# Revit family: Axis-FP
name_source: partatom
category: Оборудование
units: mm (PartAtom-declared; Revit-internal decimal feet)

## family parameters
Всегда вертикально = Да
Классификация = Нет
На основе рабочей плоскости = Нет
Общий = Нет
При загрузке вырезать с полостями = Нет
Размер круглого соединителя = Использовать диаметр
Тип детали = Нормальный
Точка принадлежности помещению = Нет

## types (239) — shared parameters
00_20_Manufacturer = BLAUBERG
00_20_Name = Axial smoke extraction fan
Casing Material = Metal, painted, grey, matt RAL 7040
Frequency = 50 Гц
Load Classification = HVAC
Maintenance zone material = <По категории>
Number of Fase = 3
Voltage = 400 В
Изготовитель = BLAUBERG
zero-valued in all types: Отметка по умолчанию

## per-type parameters (varying)
- Axis-FP-400-2D/0,55-6/25/AL: D1=450 мм; D2=490 мм; Diameter=400 мм; Dn=404 мм; Dv=390 мм; Dy=400 мм; Height=400 мм; L=400 мм; Ld=120 мм; Length=490 мм; Lv=105 мм; Maximum Air Flow=5004.0 м³/ч; Motor=Motor : 0.55 kW; N=6; P=240 мм; Power=550 Вт; W=525 мм; W1=475 мм; Weight=23.00 кг; Width=525 мм; d=8 мм; l=200 мм; l1=-200 мм; n=12; r1=225 мм
- Axis-FP-1250-4D/18,5-8/23/AL: D1=1320 мм; D2=1400 мм; Diameter=1250 мм; Dn=1254 мм; Dv=1240 мм; Dy=1250 мм; Height=750 мм; L=750 мм; Ld=225 мм; Length=1400 мм; Lv=210 мм; Maximum Air Flow=77040.0 м³/ч; Motor=Motor : 18.5 kW; N=8; P=665 мм; Power=18500 Вт; W=1450 мм; W1=1400 мм; Weight=335.00 кг; Width=1450 мм; d=15 мм; l=375 мм; l1=-375 мм; n=20; r1=660 мм
- Axis-FP-500-2D/1,1-6/25/AL: D1=560 мм; D2=600 мм; Diameter=500 мм; Dn=504 мм; Dv=490 мм; Dy=500 мм; Height=400 мм; L=400 мм; Ld=120 мм; Length=600 мм; Lv=105 мм; Maximum Air Flow=7920.0 м³/ч; Motor=Motor : 1.1 kW; N=6; P=290 мм; Power=1100 Вт; W=620 мм; W1=570 мм; Weight=32.00 кг; Width=620 мм; d=12 мм; l=200 мм; l1=-200 мм; n=12; r1=280 мм
- Axis-FP-560-2D/1,1-6/25/AL: D1=620 мм; D2=660 мм; Diameter=560 мм; Dn=564 мм; Dv=550 мм; Dy=560 мм; Height=400 мм; L=400 мм; Ld=120 мм; Length=660 мм; Lv=105 мм; Maximum Air Flow=9540.0 м³/ч; Motor=Motor : 1.1 kW; N=6; P=320 мм; Power=1100 Вт; W=680 мм; W1=630 мм; Weight=34.00 кг; Width=680 мм; d=12 мм; l=200 мм; l1=-200 мм; n=12; r1=310 мм
- Axis-FP-450-2D/0,75-6/25/AL: D1=500 мм; D2=540 мм; Diameter=450 мм; Dn=454 мм; Dv=440 мм; Dy=450 мм; Height=400 мм; L=400 мм; Ld=120 мм; Length=540 мм; Lv=105 мм; Maximum Air Flow=6480.0 м³/ч; Motor=Motor : 0.75 kW; N=6; P=265 мм; Power=750 Вт; W=580 мм; W1=530 мм; Weight=26.10 кг; Width=580 мм; d=8 мм; l=200 мм; l1=-200 мм; n=12; r1=250 мм
- Axis-FP-630-2D/2,2-6/25/AL: D1=690 мм; D2=730 мм; Diameter=630 мм; Dn=634 мм; Dv=620 мм; Dy=630 мм; Height=400 мм; L=400 мм; Ld=120 мм; Length=730 мм; Lv=105 мм; Maximum Air Flow=14040.0 м³/ч; Motor=Motor : 2.2kW; N=6; P=355 мм; Power=2200 Вт; W=750 мм; W1=700 мм; Weight=41.50 кг; Width=750 мм; d=12 мм; l=200 мм; l1=-200 мм; n=12; r1=345 мм
- Axis-FP-710-4D/0,75-6/20/AL: D1=770 мм; D2=810 мм; Diameter=710 мм; Dn=714 мм; Dv=700 мм; Dy=710 мм; Height=400 мм; L=400 мм; Ld=120 мм; Length=810 мм; Lv=105 мм; Maximum Air Flow=10440.0 м³/ч; Motor=Motor : 0.75 kW; N=6; P=395 мм; Power=750 Вт; W=845 мм; W1=795 мм; Weight=47.50 кг; Width=845 мм; d=12 мм; l=200 мм; l1=-200 мм; n=16; r1=385 мм
- Axis-FP-800-4D/1,1-6/20/AL: D1=860 мм; D2=900 мм; Diameter=800 мм; Dn=804 мм; Dv=790 мм; Dy=800 мм; Height=400 мм; L=400 мм; Ld=120 мм; Length=900 мм; Lv=105 мм; Maximum Air Flow=14040.0 м³/ч; Motor=Motor : 1.1 kW; N=6; P=440 мм; Power=1100 Вт; W=925 мм; W1=875 мм; Weight=59.50 кг; Width=925 мм; d=12 мм; l=200 мм; l1=-200 мм; n=16; r1=430 мм
- Axis-FP-900-4D/3-8/23,5/AL: D1=970 мм; D2=1015 мм; Diameter=900 мм; Dn=904 мм; Dv=890 мм; Dy=900 мм; Height=550 мм; L=550 мм; Ld=165 мм; Length=1015 мм; Lv=150 мм; Maximum Air Flow=23400.0 м³/ч; Motor=Motor : 3 kW; N=8; P=490 мм; Power=3000 Вт; W=1025 мм; W1=975 мм; Weight=92.00 кг; Width=1025 мм; d=15 мм; l=275 мм; l1=-275 мм; n=16; r1=485 мм
- Axis-FP-1000-4D/5,5-6/24/AL: D1=1070 мм; D2=1115 мм; Diameter=1000 мм; Dn=1004 мм; Dv=990 мм; Dy=1000 мм; Height=600 мм; L=600 мм; Ld=180 мм; Length=1115 мм; Lv=165 мм; Maximum Air Flow=36000.0 м³/ч; Motor=Motor : 5.5 kW; N=6; P=540 мм; Power=5500 Вт; W=1140 мм; W1=1090 мм; Weight=147.50 кг; Width=1140 мм; d=15 мм; l=300 мм; l1=-300 мм; n=16; r1=535 мм
- Axis-FP-1120-4D/7,5-6/23/AL: D1=1190 мм; D2=1270 мм; Diameter=1120 мм; Dn=1124 мм; Dv=1110 мм; Dy=1120 мм; Height=600 мм; L=600 мм; Ld=180 мм; Length=1270 мм; Lv=165 мм; Maximum Air Flow=46800.0 м³/ч; Motor=Motor : 7.5 kW; N=6; P=600 мм; Power=7500 Вт; W=1280 мм; W1=1230 мм; Weight=183.00 кг; Width=1280 мм; d=15 мм; l=300 мм; l1=-300 мм; n=20; r1=595 мм
- Axis-FP-400-2D/0,75-6/30/AL: D1=450 мм; D2=490 мм; Diameter=400 мм; Dn=404 мм; Dv=390 мм; Dy=400 мм; Height=400 мм; L=400 мм; Ld=120 мм; Length=490 мм; Lv=105 мм; Maximum Air Flow=5760.0 м³/ч; Motor=Motor : 0.75 kW; N=6; P=240 мм; Power=750 Вт; W=525 мм; W1=475 мм; Weight=24.60 кг; Width=525 мм; d=8 мм; l=200 мм; l1=-200 мм; n=12; r1=225 мм
- Axis-FP-400-2D/1,1-6/35/AL: D1=450 мм; D2=490 мм; Diameter=400 мм; Dn=404 мм; Dv=390 мм; Dy=400 мм; Height=400 мм; L=400 мм; Ld=120 мм; Length=490 мм; Lv=105 мм; Maximum Air Flow=6660.0 м³/ч; Motor=Motor : 1.1 kW; N=6; P=240 мм; Power=1100 Вт; W=525 мм; W1=475 мм; Weight=28.60 кг; Width=525 мм; d=8 мм; l=200 мм; l1=-200 мм; n=12; r1=225 мм
- Axis-FP-400-2D/1,5-6/40/AL: D1=450 мм; D2=490 мм; Diameter=400 мм; Dn=404 мм; Dv=390 мм; Dy=400 мм; Height=400 мм; L=400 мм; Ld=120 мм; Length=490 мм; Lv=105 мм; Maximum Air Flow=7200.0 м³/ч; Motor=Motor : 1.5kW; N=6; P=240 мм; Power=1500 Вт; W=525 мм; W1=475 мм; Weight=30.10 кг; Width=525 мм; d=8 мм; l=200 мм; l1=-200 мм; n=12; r1=225 мм
- Axis-FP-400-2D/1,5-6/45/AL: D1=450 мм; D2=490 мм; Diameter=400 мм; Dn=404 мм; Dv=390 мм; Dy=400 мм; Height=400 мм; L=400 мм; Ld=120 мм; Length=490 мм; Lv=105 мм; Maximum Air Flow=7920.0 м³/ч; Motor=Motor : 1.5kW; N=6; P=240 мм; Power=1500 Вт; W=525 мм; W1=475 мм; Weight=30.10 кг; Width=525 мм; d=8 мм; l=200 мм; l1=-200 мм; n=12; r1=225 мм
- Axis-FP-400-2D/2,2-8/45/AL: D1=450 мм; D2=490 мм; Diameter=400 мм; Dn=404 мм; Dv=390 мм; Dy=400 мм; Height=400 мм; L=400 мм; Ld=120 мм; Length=490 мм; Lv=105 мм; Maximum Air Flow=8280.0 м³/ч; Motor=Motor : 2.2kW; N=8; P=240 мм; Power=2200 Вт; W=525 мм; W1=475 мм; Weight=32.60 кг; Width=525 мм; d=8 мм; l=200 мм; l1=-200 мм; n=12; r1=225 мм
- Axis-FP-400-4D/0,55-6/30/AL: D1=450 мм; D2=490 мм; Diameter=400 мм; Dn=404 мм; Dv=390 мм; Dy=400 мм; Height=400 мм; L=400 мм; Ld=120 мм; Length=490 мм; Lv=105 мм; Maximum Air Flow=2880.0 м³/ч; Motor=Motor : 0.55 kW; N=6; P=240 мм; Power=550 Вт; W=525 мм; W1=475 мм; Weight=24.50 кг; Width=525 мм; d=8 мм; l=200 мм; l1=-200 мм; n=12; r1=225 мм
- Axis-FP-400-4D/0,55-6/35/AL: D1=450 мм; D2=490 мм; Diameter=400 мм; Dn=404 мм; Dv=390 мм; Dy=400 мм; Height=400 мм; L=400 мм; Ld=120 мм; Length=490 мм; Lv=105 мм; Maximum Air Flow=3420.0 м³/ч; Motor=Motor : 0.55 kW; N=6; P=240 мм; Power=550 Вт; W=525 мм; W1=475 мм; Weight=24.50 кг; Width=525 мм; d=8 мм; l=200 мм; l1=-200 мм; n=12; r1=225 мм
- Axis-FP-400-4D/0,55-6/40/AL: D1=450 мм; D2=490 мм; Diameter=400 мм; Dn=404 мм; Dv=390 мм; Dy=400 мм; Height=400 мм; L=400 мм; Ld=120 мм; Length=490 мм; Lv=105 мм; Maximum Air Flow=3600.0 м³/ч; Motor=Motor : 0.55 kW; N=6; P=240 мм; Power=550 Вт; W=525 мм; W1=475 мм; Weight=24.50 кг; Width=525 мм; d=8 мм; l=200 мм; l1=-200 мм; n=12; r1=225 мм
- Axis-FP-400-4D/0,55-6/45/AL: D1=450 мм; D2=490 мм; Diameter=400 мм; Dn=404 мм; Dv=390 мм; Dy=400 мм; Height=400 мм; L=400 мм; Ld=120 мм; Length=490 мм; Lv=105 мм; Maximum Air Flow=3780.0 м³/ч; Motor=Motor : 0.55 kW; N=6; P=240 мм; Power=550 Вт; W=525 мм; W1=475 мм; Weight=24.50 кг; Width=525 мм; d=8 мм; l=200 мм; l1=-200 мм; n=12; r1=225 мм
- Axis-FP-400-4D/0,55-8/45/AL: D1=450 мм; D2=490 мм; Diameter=400 мм; Dn=404 мм; Dv=390 мм; Dy=400 мм; Height=400 мм; L=400 мм; Ld=120 мм; Length=490 мм; Lv=105 мм; Maximum Air Flow=4140.0 м³/ч; Motor=Motor : 0.55 kW; N=8; P=240 мм; Power=550 Вт; W=525 мм; W1=475 мм; Weight=25.00 кг; Width=525 мм; d=8 мм; l=200 мм; l1=-200 мм; n=12; r1=225 мм
- Axis-FP-400-2/4D/0,8/0,2-6/30/AL: D1=450 мм; D2=490 мм; Diameter=400 мм; Dn=404 мм; Dv=390 мм; Dy=400 мм; Height=400 мм; L=400 мм; Ld=120 мм; Length=490 мм; Lv=105 мм; Maximum Air Flow=5760.0 м³/ч; Motor=Motor : 0.8 kW; N=6; P=240 мм; Power=800 Вт; W=525 мм; W1=475 мм; Weight=29.10 кг; Width=525 мм; d=8 мм; l=200 мм; l1=-200 мм; n=12; r1=225 мм
- Axis-FP-400-2/4D/1,1/0,25-6/35/AL: D1=450 мм; D2=490 мм; Diameter=400 мм; Dn=404 мм; Dv=390 мм; Dy=400 мм; Height=400 мм; L=400 мм; Ld=120 мм; Length=490 мм; Lv=105 мм; Maximum Air Flow=6660.0 м³/ч; Motor=Motor : 1.1 kW; N=6; P=240 мм; Power=1100 Вт; W=525 мм; W1=475 мм; Weight=30.10 кг; Width=525 мм; d=8 мм; l=200 мм; l1=-200 мм; n=12; r1=225 мм
- Axis-FP-400-2/4D/1,5/0,37-6/40/AL: D1=450 мм; D2=490 мм; Diameter=400 мм; Dn=404 мм; Dv=390 мм; Dy=400 мм; Height=400 мм; L=400 мм; Ld=120 мм; Length=490 мм; Lv=105 мм; Maximum Air Flow=7200.0 м³/ч; Motor=Motor : 1.5kW; N=6; P=240 мм; Power=1100 Вт; W=525 мм; W1=475 мм; Weight=35.80 кг; Width=525 мм; d=8 мм; l=200 мм; l1=-200 мм; n=12; r1=225 мм
- Axis-FP-400-2/4D/1,5/0,37-6/45/AL: D1=450 мм; D2=490 мм; Diameter=400 мм; Dn=404 мм; Dv=390 мм; Dy=400 мм; Height=400 мм; L=400 мм; Ld=120 мм; Length=490 мм; Lv=105 мм; Maximum Air Flow=7920.0 м³/ч; Motor=Motor : 1.5kW; N=6; P=240 мм; Power=1500 Вт; W=525 мм; W1=475 мм; Weight=35.80 кг; Width=525 мм; d=8 мм; l=200 мм; l1=-200 мм; n=12; r1=225 мм
- Axis-FP-400-2/4D/2,2/0,5-8/45/AL: D1=450 мм; D2=490 мм; Diameter=400 мм; Dn=404 мм; Dv=390 мм; Dy=400 мм; Height=400 мм; L=400 мм; Ld=120 мм; Length=490 мм; Lv=105 мм; Maximum Air Flow=8100.0 м³/ч; Motor=Motor : 2.2kW; N=8; P=240 мм; Power=2200 Вт; W=525 мм; W1=475 мм; Weight=38.00 кг; Width=525 мм; d=8 мм; l=200 мм; l1=-200 мм; n=12; r1=225 мм
- Axis-FP-450-2D/1,1-6/30/AL: D1=500 мм; D2=540 мм; Diameter=450 мм; Dn=454 мм; Dv=440 мм; Dy=450 мм; Height=400 мм; L=400 мм; Ld=120 мм; Length=540 мм; Lv=105 мм; Maximum Air Flow=7812.0 м³/ч; Motor=Motor : 1.1 kW; N=6; P=265 мм; Power=1100 Вт; W=580 мм; W1=530 мм; Weight=30.10 кг; Width=580 мм; d=8 мм; l=200 мм; l1=-200 мм; n=12; r1=250 мм
- Axis-FP-450-2D/1,5-6/35/AL: D1=500 мм; D2=540 мм; Diameter=450 мм; Dn=454 мм; Dv=440 мм; Dy=450 мм; Height=400 мм; L=400 мм; Ld=120 мм; Length=540 мм; Lv=105 мм; Maximum Air Flow=9360.0 м³/ч; Motor=Motor : 1.5kW; N=6; P=265 мм; Power=1500 Вт; W=580 мм; W1=530 мм; Weight=31.60 кг; Width=580 мм; d=8 мм; l=200 мм; l1=-200 мм; n=12; r1=250 мм
- Axis-FP-450-2D/2,2-6/40/AL: D1=500 мм; D2=540 мм; Diameter=450 мм; Dn=454 мм; Dv=440 мм; Dy=450 мм; Height=400 мм; L=400 мм; Ld=120 мм; Length=540 мм; Lv=105 мм; Maximum Air Flow=10080.0 м³/ч; Motor=Motor : 2.2kW; N=6; P=265 мм; Power=2200 Вт; W=580 мм; W1=530 мм; Weight=34.00 кг; Width=580 мм; d=8 мм; l=200 мм; l1=-200 мм; n=12; r1=250 мм
- Axis-FP-450-2D/3-8/40/AL: D1=500 мм; D2=540 мм; Diameter=450 мм; Dn=454 мм; Dv=440 мм; Dy=450 мм; Height=400 мм; L=400 мм; Ld=120 мм; Length=540 мм; Lv=105 мм; Maximum Air Flow=10440.0 м³/ч; Motor=Motor : 3 kW; N=6; P=265 мм; Power=3000 Вт; W=580 мм; W1=530 мм; Weight=34.00 кг; Width=580 мм; d=8 мм; l=200 мм; l1=-200 мм; n=12; r1=250 мм
- Axis-FP-450-2D/4-8/45/AL: D1=500 мм; D2=540 мм; Diameter=450 мм; Dn=454 мм; Dv=440 мм; Dy=450 мм; Height=400 мм; L=400 мм; Ld=120 мм; Length=540 мм; Lv=105 мм; Maximum Air Flow=11880.0 м³/ч; Motor=Motor : 3 kW; N=8; P=265 мм; Power=4000 Вт; W=580 мм; W1=530 мм; Weight=52.80 кг; Width=580 мм; d=8 мм; l=200 мм; l1=-200 мм; n=12; r1=250 мм
- Axis-FP-450-4D/0,55-6/25/AL: D1=500 мм; D2=540 мм; Diameter=450 мм; Dn=454 мм; Dv=440 мм; Dy=450 мм; Height=400 мм; L=400 мм; Ld=120 мм; Length=540 мм; Lv=105 мм; Maximum Air Flow=2304.0 м³/ч; Motor=Motor : 0.55 kW; N=6; P=265 мм; Power=550 Вт; W=580 мм; W1=530 мм; Weight=24.60 кг; Width=580 мм; d=8 мм; l=200 мм; l1=-200 мм; n=12; r1=250 мм
- Axis-FP-450-4D/0,55-6/30/AL: D1=500 мм; D2=540 мм; Diameter=450 мм; Dn=454 мм; Dv=440 мм; Dy=450 мм; Height=400 мм; L=400 мм; Ld=120 мм; Length=540 мм; Lv=105 мм; Maximum Air Flow=3780.0 м³/ч; Motor=Motor : 0.55 kW; N=6; P=265 мм; Power=550 Вт; W=580 мм; W1=530 мм; Weight=24.60 кг; Width=580 мм; d=8 мм; l=200 мм; l1=-200 мм; n=12; r1=250 мм
- Axis-FP-450-4D/0,55-6/35/AL: D1=500 мм; D2=540 мм; Diameter=450 мм; Dn=454 мм; Dv=440 мм; Dy=450 мм; Height=400 мм; L=400 мм; Ld=120 мм; Length=540 мм; Lv=105 мм; Maximum Air Flow=4500.0 м³/ч; Motor=Motor : 0.55 kW; N=6; P=265 мм; Power=550 Вт; W=580 мм; W1=530 мм; Weight=24.60 кг; Width=580 мм; d=8 мм; l=200 мм; l1=-200 мм; n=12; r1=250 мм
- Axis-FP-450-4D/0,55-6/40/AL: D1=500 мм; D2=540 мм; Diameter=450 мм; Dn=454 мм; Dv=440 мм; Dy=450 мм; Height=400 мм; L=400 мм; Ld=120 мм; Length=540 мм; Lv=105 мм; Maximum Air Flow=5040.0 м³/ч; Motor=Motor : 0.55 kW; N=6; P=265 мм; Power=550 Вт; W=580 мм; W1=530 мм; Weight=24.60 кг; Width=580 мм; d=8 мм; l=200 мм; l1=-200 мм; n=12; r1=250 мм
- Axis-FP-450-4D/0,55-8/40/AL: D1=500 мм; D2=540 мм; Diameter=450 мм; Dn=454 мм; Dv=440 мм; Dy=450 мм; Height=400 мм; L=400 мм; Ld=120 мм; Length=540 мм; Lv=105 мм; Maximum Air Flow=5220.0 м³/ч; Motor=Motor : 0.55 kW; N=8; P=265 мм; Power=550 Вт; W=580 мм; W1=530 мм; Weight=24.60 кг; Width=580 мм; d=8 мм; l=200 мм; l1=-200 мм; n=12; r1=250 мм
- Axis-FP-450-4D/0,55-8/45/AL: D1=500 мм; D2=540 мм; Diameter=450 мм; Dn=454 мм; Dv=440 мм; Dy=450 мм; Height=400 мм; L=400 мм; Ld=120 мм; Length=540 мм; Lv=105 мм; Maximum Air Flow=5940.0 м³/ч; Motor=Motor : 0.55 kW; N=8; P=265 мм; Power=550 Вт; W=580 мм; W1=530 мм; Weight=24.60 кг; Width=580 мм; d=8 мм; l=200 мм; l1=-200 мм; n=12; r1=250 мм
- Axis-FP-450-2/4D/4,4/1,1-8/45/AL: D1=500 мм; D2=540 мм; Diameter=450 мм; Dn=454 мм; Dv=440 мм; Dy=450 мм; Height=400 мм; L=400 мм; Ld=120 мм; Length=540 мм; Lv=105 мм; Maximum Air Flow=11880.0 м³/ч; Motor=Motor : 4.4 kW; N=8; P=265 мм; Power=4400 Вт; W=580 мм; W1=530 мм; Weight=63.80 кг; Width=580 мм; d=8 мм; l=200 мм; l1=-200 мм; n=12; r1=250 мм
- Axis-FP-450-2/4D/3,1/0,8-8/40/AL: D1=500 мм; D2=540 мм; Diameter=450 мм; Dn=454 мм; Dv=440 мм; Dy=450 мм; Height=400 мм; L=400 мм; Ld=120 мм; Length=540 мм; Lv=105 мм; Maximum Air Flow=10440.0 м³/ч; Motor=Motor : 3.1 kW; N=8; P=265 мм; Power=3100 Вт; W=580 мм; W1=530 мм; Weight=51.90 кг; Width=580 мм; d=8 мм; l=200 мм; l1=-200 мм; n=12; r1=250 мм
- Axis-FP-450-2/4D/2,2/0,5-6/40/AL: D1=500 мм; D2=540 мм; Diameter=450 мм; Dn=454 мм; Dv=440 мм; Dy=450 мм; Height=400 мм; L=400 мм; Ld=120 мм; Length=540 мм; Lv=105 мм; Maximum Air Flow=10080.0 м³/ч; Motor=Motor : 2.2kW; N=6; P=265 мм; Power=2200 Вт; W=580 мм; W1=530 мм; Weight=39.30 кг; Width=580 мм; d=8 мм; l=200 мм; l1=-200 мм; n=12; r1=250 мм
- Axis-FP-450-2/4D/1,5/0,37-6/35/AL: D1=500 мм; D2=540 мм; Diameter=450 мм; Dn=454 мм; Dv=440 мм; Dy=450 мм; Height=400 мм; L=400 мм; Ld=120 мм; Length=540 мм; Lv=105 мм; Maximum Air Flow=9000.0 м³/ч; Motor=Motor : 1.5kW; N=6; P=265 мм; Power=1500 Вт; W=580 мм; W1=530 мм; Weight=37.30 кг; Width=580 мм; d=8 мм; l=200 мм; l1=-200 мм; n=12; r1=250 мм
- Axis-FP-450-2/4D/1,1/0,25-6/30/AL: D1=500 мм; D2=540 мм; Diameter=450 мм; Dn=454 мм; Dv=440 мм; Dy=450 мм; Height=400 мм; L=400 мм; Ld=120 мм; Length=540 мм; Lv=105 мм; Maximum Air Flow=7740.0 м³/ч; Motor=Motor : 1.1 kW; N=6; P=265 мм; Power=1100 Вт; W=580 мм; W1=530 мм; Weight=31.60 кг; Width=580 мм; d=8 мм; l=200 мм; l1=-200 мм; n=12; r1=250 мм
- Axis-FP-450-2/4D/0,8/0,2-6/25/AL: D1=500 мм; D2=540 мм; Diameter=450 мм; Dn=454 мм; Dv=440 мм; Dy=450 мм; Height=400 мм; L=400 мм; Ld=120 мм; Length=540 мм; Lv=105 мм; Maximum Air Flow=6480.0 м³/ч; Motor=Motor : 0.8 kW; N=6; P=265 мм; Power=800 Вт; W=580 мм; W1=530 мм; Weight=30.60 кг; Width=580 мм; d=8 мм; l=200 мм; l1=-200 мм; n=12; r1=250 мм
- Axis-FP-500-2D/1,5-6/30/AL: D1=560 мм; D2=600 мм; Diameter=500 мм; Dn=504 мм; Dv=490 мм; Dy=500 мм; Height=400 мм; L=400 мм; Ld=120 мм; Length=600 мм; Lv=105 мм; Maximum Air Flow=9540.0 м³/ч; Motor=Motor : 1.5kW; N=6; P=290 мм; Power=1500 Вт; W=620 мм; W1=570 мм; Weight=33.50 кг; Width=620 мм; d=12 мм; l=200 мм; l1=-200 мм; n=12; r1=280 мм
- Axis-FP-500-2D/2,2-6/35/AL: D1=560 мм; D2=600 мм; Diameter=500 мм; Dn=504 мм; Dv=490 мм; Dy=500 мм; Height=400 мм; L=400 мм; Ld=120 мм; Length=600 мм; Lv=105 мм; Maximum Air Flow=11520.0 м³/ч; Motor=Motor : 2.2kW; N=6; P=290 мм; Power=2200 Вт; W=620 мм; W1=570 мм; Weight=36.00 кг; Width=620 мм; d=12 мм; l=200 мм; l1=-200 мм; n=12; r1=280 мм
- Axis-FP-500-2D/3-8/35/AL: D1=560 мм; D2=600 мм; Diameter=500 мм; Dn=504 мм; Dv=490 мм; Dy=500 мм; Height=400 мм; L=400 мм; Ld=120 мм; Length=600 мм; Lv=105 мм; Maximum Air Flow=12600.0 м³/ч; Motor=Motor : 3 kW; N=8; P=290 мм; Power=3000 Вт; W=620 мм; W1=570 мм; Weight=43.00 кг; Width=620 мм; d=12 мм; l=200 мм; l1=-200 мм; n=12; r1=280 мм
- Axis-FP-500-2D/4-8/40/AL: D1=560 мм; D2=600 мм; Diameter=500 мм; Dn=504 мм; Dv=490 мм; Dy=500 мм; Height=500 мм; L=500 мм; Ld=150 мм; Length=600 мм; Lv=135 мм; Maximum Air Flow=14040.0 м³/ч; Motor=Motor : 4 kW; N=8; P=290 мм; Power=4000 Вт; W=620 мм; W1=570 мм; Weight=55.00 кг; Width=620 мм; d=12 мм; l=250 мм; l1=-250 мм; n=12; r1=280 мм
- Axis-FP-500-2D/5,5-8/45/AL: D1=560 мм; D2=600 мм; Diameter=500 мм; Dn=504 мм; Dv=490 мм; Dy=500 мм; Height=500 мм; L=500 мм; Ld=150 мм; Length=600 мм; Lv=135 мм; Maximum Air Flow=15480.0 м³/ч; Motor=Motor : 5.5 kW; N=8; P=290 мм; Power=5500 Вт; W=620 мм; W1=570 мм; Weight=63.00 кг; Width=620 мм; d=12 мм; l=250 мм; l1=-250 мм; n=12; r1=280 мм
- Axis-FP-500-4D/0,55-6/25/AL: D1=560 мм; D2=600 мм; Diameter=500 мм; Dn=504 мм; Dv=490 мм; Dy=500 мм; Height=400 мм; L=400 мм; Ld=120 мм; Length=600 мм; Lv=105 мм; Maximum Air Flow=3960.0 м³/ч; Motor=Motor : 0.55 kW; N=6; P=290 мм; Power=550 Вт; W=620 мм; W1=570 мм; Weight=28.00 кг; Width=620 мм; d=12 мм; l=200 мм; l1=-200 мм; n=12; r1=280 мм
- Axis-FP-500-4D/0,55-6/30/AL: D1=560 мм; D2=600 мм; Diameter=500 мм; Dn=504 мм; Dv=490 мм; Dy=500 мм; Height=400 мм; L=400 мм; Ld=120 мм; Length=600 мм; Lv=105 мм; Maximum Air Flow=4860.0 м³/ч; Motor=Motor : 0.55 kW; N=6; P=290 мм; Power=550 Вт; W=620 мм; W1=570 мм; Weight=28.00 кг; Width=620 мм; d=12 мм; l=200 мм; l1=-200 мм; n=12; r1=280 мм
- Axis-FP-500-4D/0,55-6/35/AL: D1=560 мм; D2=600 мм; Diameter=500 мм; Dn=504 мм; Dv=490 мм; Dy=500 мм; Height=400 мм; L=400 мм; Ld=120 мм; Length=600 мм; Lv=105 мм; Maximum Air Flow=5940.0 м³/ч; Motor=Motor : 0.55 kW; N=6; P=290 мм; Power=550 Вт; W=620 мм; W1=570 мм; Weight=28.00 кг; Width=620 мм; d=12 мм; l=200 мм; l1=-200 мм; n=12; r1=280 мм
- Axis-FP-500-4D/0,55-6/40/AL: D1=560 мм; D2=600 мм; Diameter=500 мм; Dn=504 мм; Dv=490 мм; Dy=500 мм; Height=400 мм; L=400 мм; Ld=120 мм; Length=600 мм; Lv=105 мм; Maximum Air Flow=6408.0 м³/ч; Motor=Motor : 0.55 kW; N=6; P=290 мм; Power=550 Вт; W=620 мм; W1=570 мм; Weight=28.00 кг; Width=620 мм; d=12 мм; l=200 мм; l1=-200 мм; n=12; r1=280 мм
- Axis-FP-500-4D/0,55-6/45/AL: D1=560 мм; D2=600 мм; Diameter=500 мм; Dn=504 мм; Dv=490 мм; Dy=500 мм; Height=400 мм; L=400 мм; Ld=120 мм; Length=600 мм; Lv=105 мм; Maximum Air Flow=7020.0 м³/ч; Motor=Motor : 0.55 kW; N=6; P=290 мм; Power=550 Вт; W=620 мм; W1=570 мм; Weight=28.00 кг; Width=620 мм; d=12 мм; l=200 мм; l1=-200 мм; n=12; r1=280 мм
- Axis-FP-500-4D/0,75-8/45/AL: D1=560 мм; D2=600 мм; Diameter=500 мм; Dn=504 мм; Dv=490 мм; Dy=500 мм; Height=400 мм; L=400 мм; Ld=120 мм; Length=600 мм; Lv=105 мм; Maximum Air Flow=7560.0 м³/ч; Motor=Motor : 0.75 kW; N=8; P=290 мм; Power=750 Вт; W=620 мм; W1=570 мм; Weight=29.50 кг; Width=620 мм; d=12 мм; l=200 мм; l1=-200 мм; n=12; r1=280 мм
- Axis-FP-500-2/4D/1,1/0,25-6/25/AL: D1=560 мм; D2=600 мм; Diameter=500 мм; Dn=504 мм; Dv=490 мм; Dy=500 мм; Height=400 мм; L=400 мм; Ld=120 мм; Length=600 мм; Lv=105 мм; Maximum Air Flow=7920.0 м³/ч; Motor=Motor : 1.1 kW; N=6; P=290 мм; Power=1100 Вт; W=620 мм; W1=570 мм; Weight=29.50 кг; Width=620 мм; d=12 мм; l=200 мм; l1=-200 мм; n=12; r1=280 мм
- Axis-FP-500-2/4D/1,5/0,37-6/30/AL: D1=560 мм; D2=600 мм; Diameter=500 мм; Dn=504 мм; Dv=490 мм; Dy=500 мм; Height=400 мм; L=400 мм; Ld=120 мм; Length=600 мм; Lv=105 мм; Maximum Air Flow=9540.0 м³/ч; Motor=Motor : 1.5kW; N=6; P=290 мм; Power=1500 Вт; W=620 мм; W1=570 мм; Weight=39.00 кг; Width=620 мм; d=12 мм; l=200 мм; l1=-200 мм; n=12; r1=280 мм
- Axis-FP-500-2/4D/2,2/0,5-6/35/AL: D1=560 мм; D2=600 мм; Diameter=500 мм; Dn=504 мм; Dv=490 мм; Dy=500 мм; Height=400 мм; L=400 мм; Ld=120 мм; Length=600 мм; Lv=105 мм; Maximum Air Flow=11520.0 м³/ч; Motor=Motor : 2.2kW; N=6; P=290 мм; Power=2200 Вт; W=620 мм; W1=570 мм; Weight=41.00 кг; Width=620 мм; d=12 мм; l=200 мм; l1=-200 мм; n=12; r1=280 мм
- Axis-FP-500-2/4D/3,1/0,8-8/35/AL: D1=560 мм; D2=600 мм; Diameter=500 мм; Dn=504 мм; Dv=490 мм; Dy=500 мм; Height=500 мм; L=500 мм; Ld=150 мм; Length=600 мм; Lv=135 мм; Maximum Air Flow=12960.0 м³/ч; Motor=Motor : 3.1 kW; N=8; P=290 мм; Power=3100 Вт; W=620 мм; W1=570 мм; Weight=54.00 кг; Width=620 мм; d=12 мм; l=250 мм; l1=-250 мм; n=12; r1=280 мм
- Axis-FP-500-2/4D/4,4/1,1-8/40/AL: D1=560 мм; D2=600 мм; Diameter=500 мм; Dn=504 мм; Dv=490 мм; Dy=500 мм; Height=500 мм; L=500 мм; Ld=150 мм; Length=600 мм; Lv=135 мм; Maximum Air Flow=14040.0 м³/ч; Motor=Motor : 4.4 kW; N=8; P=290 мм; Power=4400 Вт; W=620 мм; W1=570 мм; Weight=66.00 кг; Width=620 мм; d=12 мм; l=250 мм; l1=-250 мм; n=12; r1=280 мм
- Axis-FP-500-2/4D/6/1,5-8/45/AL: D1=560 мм; D2=600 мм; Diameter=500 мм; Dn=504 мм; Dv=490 мм; Dy=500 мм; Height=550 мм; L=550 мм; Ld=165 мм; Length=600 мм; Lv=150 мм; Maximum Air Flow=15480.0 м³/ч; Motor=Motor : 6 kW; N=8; P=290 мм; Power=6000 Вт; W=620 мм; W1=570 мм; Weight=85.00 кг; Width=620 мм; d=12 мм; l=275 мм; l1=-275 мм; n=12; r1=280 мм
- Axis-FP-560-2D/1,5-6/30/AL: D1=620 мм; D2=660 мм; Diameter=560 мм; Dn=564 мм; Dv=550 мм; Dy=560 мм; Height=400 мм; L=400 мм; Ld=120 мм; Length=660 мм; Lv=105 мм; Maximum Air Flow=11880.0 м³/ч; Motor=Motor : 1.5kW; N=6; P=320 мм; Power=1500 Вт; W=680 мм; W1=630 мм; Weight=35.50 кг; Width=680 мм; d=12 мм; l=200 мм; l1=-200 мм; n=12; r1=310 мм
- Axis-FP-560-2D/2,2-8/30/AL: D1=620 мм; D2=660 мм; Diameter=560 мм; Dn=564 мм; Dv=550 мм; Dy=560 мм; Height=400 мм; L=400 мм; Ld=120 мм; Length=660 мм; Lv=105 мм; Maximum Air Flow=13500.0 м³/ч; Motor=Motor : 2.2kW; N=8; P=320 мм; Power=2200 Вт; W=680 мм; W1=630 мм; Weight=38.00 кг; Width=680 мм; d=12 мм; l=200 мм; l1=-200 мм; n=12; r1=310 мм
- Axis-FP-560-2D/4-8/35/AL: D1=620 мм; D2=660 мм; Diameter=560 мм; Dn=564 мм; Dv=550 мм; Dy=560 мм; Height=500 мм; L=500 мм; Ld=150 мм; Length=660 мм; Lv=135 мм; Maximum Air Flow=16488.0 м³/ч; Motor=Motor : 4 kW; N=8; P=320 мм; Power=4000 Вт; W=680 мм; W1=630 мм; Weight=57.50 кг; Width=680 мм; d=12 мм; l=250 мм; l1=-250 мм; n=12; r1=310 мм
- Axis-FP-560-2D/5,5-8/40/AL: D1=620 мм; D2=660 мм; Diameter=560 мм; Dn=564 мм; Dv=550 мм; Dy=560 мм; Height=500 мм; L=500 мм; Ld=150 мм; Length=660 мм; Lv=135 мм; Maximum Air Flow=18000.0 м³/ч; Motor=Motor : 5.5 kW; N=8; P=320 мм; Power=5500 Вт; W=680 мм; W1=630 мм; Weight=65.50 кг; Width=680 мм; d=12 мм; l=250 мм; l1=-250 мм; n=12; r1=310 мм
- Axis-FP-560-2D/7,5-8/45/AL: D1=620 мм; D2=660 мм; Diameter=560 мм; Dn=564 мм; Dv=550 мм; Dy=560 мм; Height=500 мм; L=500 мм; Ld=150 мм; Length=660 мм; Lv=135 мм; Maximum Air Flow=20520.0 м³/ч; Motor=Motor : 7.5 kW; N=8; P=320 мм; Power=7500 Вт; W=680 мм; W1=630 мм; Weight=67.50 кг; Width=680 мм; d=12 мм; l=250 мм; l1=-250 мм; n=12; r1=310 мм
- Axis-FP-560-4D/0,55-6/25/AL: D1=620 мм; D2=660 мм; Diameter=560 мм; Dn=564 мм; Dv=550 мм; Dy=560 мм; Height=400 мм; L=400 мм; Ld=120 мм; Length=660 мм; Lv=105 мм; Maximum Air Flow=4860.0 м³/ч; Motor=Motor : 0.55 kW; N=6; P=320 мм; Power=550 Вт; W=680 мм; W1=630 мм; Weight=30.00 кг; Width=680 мм; d=12 мм; l=200 мм; l1=-200 мм; n=12; r1=310 мм
- Axis-FP-560-4D/0,55-6/30/AL: D1=620 мм; D2=660 мм; Diameter=560 мм; Dn=564 мм; Dv=550 мм; Dy=560 мм; Height=400 мм; L=400 мм; Ld=120 мм; Length=660 мм; Lv=105 мм; Maximum Air Flow=5940.0 м³/ч; Motor=Motor : 0.55 kW; N=6; P=320 мм; Power=550 Вт; W=680 мм; W1=630 мм; Weight=30.00 кг; Width=680 мм; d=12 мм; l=200 мм; l1=-200 мм; n=12; r1=310 мм
- Axis-FP-560-4D/0,55-6/35/AL: D1=620 мм; D2=660 мм; Diameter=560 мм; Dn=564 мм; Dv=550 мм; Dy=560 мм; Height=400 мм; L=400 мм; Ld=120 мм; Length=660 мм; Lv=105 мм; Maximum Air Flow=7380.0 м³/ч; Motor=Motor : 0.55 kW; N=6; P=320 мм; Power=550 Вт; W=680 мм; W1=630 мм; Weight=30.00 кг; Width=680 мм; d=12 мм; l=200 мм; l1=-200 мм; n=12; r1=310 мм
- Axis-FP-560-4D/0,55-6/40/AL: D1=620 мм; D2=660 мм; Diameter=560 мм; Dn=564 мм; Dv=550 мм; Dy=560 мм; Height=400 мм; L=400 мм; Ld=120 мм; Length=660 мм; Lv=105 мм; Maximum Air Flow=8280.0 м³/ч; Motor=Motor : 0.55 kW; N=6; P=320 мм; Power=550 Вт; W=680 мм; W1=630 мм; Weight=30.00 кг; Width=680 мм; d=12 мм; l=200 мм; l1=-200 мм; n=12; r1=310 мм
- Axis-FP-560-4D/0,55-6/45/AL: D1=620 мм; D2=660 мм; Diameter=560 мм; Dn=564 мм; Dv=550 мм; Dy=560 мм; Height=400 мм; L=400 мм; Ld=120 мм; Length=660 мм; Lv=105 мм; Maximum Air Flow=9000.0 м³/ч; Motor=Motor : 0.55 kW; N=6; P=320 мм; Power=550 Вт; W=680 мм; W1=630 мм; Weight=30.00 кг; Width=680 мм; d=12 мм; l=200 мм; l1=-200 мм; n=12; r1=310 мм
- Axis-FP-560-4D/0,75-8/45/AL: D1=620 мм; D2=660 мм; Diameter=560 мм; Dn=564 мм; Dv=550 мм; Dy=560 мм; Height=400 мм; L=400 мм; Ld=120 мм; Length=660 мм; Lv=105 мм; Maximum Air Flow=10260.0 м³/ч; Motor=Motor : 0.75 kW; N=8; P=320 мм; Power=750 Вт; W=680 мм; W1=630 мм; Weight=31.50 кг; Width=680 мм; d=12 мм; l=200 мм; l1=-200 мм; n=12; r1=310 мм
- Axis-FP-560-2/4D/1,1/0,25-6/25/AL: D1=620 мм; D2=660 мм; Diameter=560 мм; Dn=564 мм; Dv=550 мм; Dy=560 мм; Height=400 мм; L=400 мм; Ld=120 мм; Length=660 мм; Lv=105 мм; Maximum Air Flow=9720.0 м³/ч; Motor=Motor : 1.1 kW; N=6; P=320 мм; Power=1100 Вт; W=680 мм; W1=630 мм; Weight=35.50 кг; Width=680 мм; d=12 мм; l=200 мм; l1=-200 мм; n=12; r1=310 мм
- Axis-FP-560-2/4D/1,5/0,37-6/30/AL: D1=620 мм; D2=660 мм; Diameter=560 мм; Dn=564 мм; Dv=550 мм; Dy=560 мм; Height=400 мм; L=400 мм; Ld=120 мм; Length=660 мм; Lv=105 мм; Maximum Air Flow=11880.0 м³/ч; Motor=Motor : 1.5kW; N=6; P=320 мм; Power=1500 Вт; W=680 мм; W1=630 мм; Weight=41.00 кг; Width=680 мм; d=12 мм; l=200 мм; l1=-200 мм; n=12; r1=310 мм
- Axis-FP-560-2/4D/2,2/0,5-8/30/AL: D1=620 мм; D2=660 мм; Diameter=560 мм; Dn=564 мм; Dv=550 мм; Dy=560 мм; Height=400 мм; L=400 мм; Ld=120 мм; Length=660 мм; Lv=105 мм; Maximum Air Flow=13500.0 м³/ч; Motor=Motor : 2.2kW; N=8; P=320 мм; Power=2200 Вт; W=680 мм; W1=630 мм; Weight=43.50 кг; Width=680 мм; d=12 мм; l=200 мм; l1=-200 мм; n=12; r1=310 мм
- Axis-FP-560-2/4D/4,4/1,1-8/35/AL: D1=620 мм; D2=660 мм; Diameter=560 мм; Dn=564 мм; Dv=550 мм; Dy=560 мм; Height=500 мм; L=500 мм; Ld=150 мм; Length=660 мм; Lv=135 мм; Maximum Air Flow=16560.0 м³/ч; Motor=Motor : 4.4 kW; N=8; P=320 мм; Power=4400 Вт; W=680 мм; W1=630 мм; Weight=68.50 кг; Width=680 мм; d=12 мм; l=250 мм; l1=-250 мм; n=12; r1=310 мм
- Axis-FP-560-2/4D/6/1,5-8/40/AL: D1=620 мм; D2=660 мм; Diameter=560 мм; Dn=564 мм; Dv=550 мм; Dy=560 мм; Height=550 мм; L=550 мм; Ld=165 мм; Length=660 мм; Lv=150 мм; Maximum Air Flow=18000.0 м³/ч; Motor=Motor : 6 kW; N=8; P=320 мм; Power=6000 Вт; W=680 мм; W1=630 мм; Weight=96.50 кг; Width=680 мм; d=12 мм; l=275 мм; l1=-275 мм; n=12; r1=310 мм
- Axis-FP-560-2/4D/8/2-8/45/AL: D1=620 мм; D2=660 мм; Diameter=560 мм; Dn=564 мм; Dv=550 мм; Dy=560 мм; Height=550 мм; L=550 мм; Ld=165 мм; Length=660 мм; Lv=150 мм; Maximum Air Flow=20520.0 м³/ч; Motor=Motor : 8 кВт; N=8; P=320 мм; Power=8000 Вт; W=680 мм; W1=630 мм; Weight=105.50 кг; Width=680 мм; d=12 мм; l=275 мм; l1=-275 мм; n=12; r1=310 мм
- Axis-FP-630-2D/3-6/30/AL: D1=690 мм; D2=730 мм; Diameter=630 мм; Dn=634 мм; Dv=620 мм; Dy=630 мм; Height=400 мм; L=400 мм; Ld=120 мм; Length=730 мм; Lv=105 мм; Maximum Air Flow=16920.0 м³/ч; Motor=Motor : 3 kW; N=6; P=355 мм; Power=3000 Вт; W=750 мм; W1=700 мм; Weight=48.00 кг; Width=750 мм; d=12 мм; l=200 мм; l1=-200 мм; n=12; r1=345 мм
- Axis-FP-630-2D/4-7/32,5/AL: D1=690 мм; D2=730 мм; Diameter=630 мм; Dn=634 мм; Dv=620 мм; Dy=630 мм; Height=500 мм; L=500 мм; Ld=150 мм; Length=730 мм; Lv=135 мм; Maximum Air Flow=18900.0 м³/ч; Motor=Motor : 4 kW; N=7; P=355 мм; Power=4000 Вт; W=750 мм; W1=700 мм; Weight=61.50 кг; Width=750 мм; d=12 мм; l=250 мм; l1=-250 мм; n=12; r1=345 мм
- Axis-FP-630-2D/5,5-7/35/AL: D1=690 мм; D2=730 мм; Diameter=630 мм; Dn=634 мм; Dv=620 мм; Dy=630 мм; Height=500 мм; L=500 мм; Ld=150 мм; Length=730 мм; Lv=135 мм; Maximum Air Flow=21060.0 м³/ч; Motor=Motor : 5.5 kW; N=7; P=355 мм; Power=5500 Вт; W=750 мм; W1=700 мм; Weight=70.00 кг; Width=750 мм; d=12 мм; l=250 мм; l1=-250 мм; n=12; r1=345 мм
- Axis-FP-630-2D/5,5-7/37,5/AL: D1=690 мм; D2=730 мм; Diameter=630 мм; Dn=634 мм; Dv=620 мм; Dy=630 мм; Height=500 мм; L=500 мм; Ld=150 мм; Length=730 мм; Lv=135 мм; Maximum Air Flow=21960.0 м³/ч; Motor=Motor : 5.5 kW; N=7; P=355 мм; Power=5500 Вт; W=750 мм; W1=700 мм; Weight=70.00 кг; Width=750 мм; d=12 мм; l=250 мм; l1=-250 мм; n=12; r1=345 мм
- Axis-FP-630-2D/7,5-7/41,5/AL: D1=690 мм; D2=730 мм; Diameter=630 мм; Dn=634 мм; Dv=620 мм; Dy=630 мм; Height=500 мм; L=500 мм; Ld=150 мм; Length=730 мм; Lv=135 мм; Maximum Air Flow=21960.0 м³/ч; Motor=Motor : 7.5 kW; N=7; P=355 мм; Power=7500 Вт; W=750 мм; W1=700 мм; Weight=71.50 кг; Width=750 мм; d=12 мм; l=250 мм; l1=-250 мм; n=12; r1=345 мм
- Axis-FP-630-2D/11-8/41,5/AL: D1=690 мм; D2=730 мм; Diameter=630 мм; Dn=634 мм; Dv=620 мм; Dy=630 мм; Height=550 мм; L=550 мм; Ld=165 мм; Length=730 мм; Lv=150 мм; Maximum Air Flow=26100.0 м³/ч; Motor=Motor : 11 kW; N=8; P=355 мм; Power=11000 Вт; W=750 мм; W1=700 мм; Weight=119.50 кг; Width=750 мм; d=12 мм; l=275 мм; l1=-275 мм; n=12; r1=345 мм
- Axis-FP-630-2D/15-8/46,5/AL: D1=690 мм; D2=730 мм; Diameter=630 мм; Dn=634 мм; Dv=620 мм; Dy=630 мм; Height=700 мм; L=700 мм; Ld=210 мм; Length=730 мм; Lv=195 мм; Maximum Air Flow=28800.0 м³/ч; Motor=Motor : 15 kW; N=8; P=355 мм; Power=15000 Вт; W=750 мм; W1=700 мм; Weight=167.00 кг; Width=750 мм; d=12 мм; l=350 мм; l1=-350 мм; n=12; r1=345 мм
- Axis-FP-630-2D/15-9/48,5/AL: D1=690 мм; D2=730 мм; Diameter=630 мм; Dn=634 мм; Dv=620 мм; Dy=630 мм; Height=700 мм; L=700 мм; Ld=210 мм; Length=730 мм; Lv=195 мм; Maximum Air Flow=30060.0 м³/ч; Motor=Motor : 15 kW; N=9; P=355 мм; Power=15000 Вт; W=750 мм; W1=700 мм; Weight=166.00 кг; Width=750 мм; d=12 мм; l=350 мм; l1=-350 мм; n=12; r1=345 мм
- Axis-FP-630-4D/0,55-8/25/AL: D1=690 мм; D2=730 мм; Diameter=630 мм; Dn=634 мм; Dv=620 мм; Dy=630 мм; Height=400 мм; L=400 мм; Ld=120 мм; Length=730 мм; Lv=105 мм; Maximum Air Flow=6480.0 м³/ч; Motor=Motor : 0.55 kW; N=8; P=355 мм; Power=550 Вт; W=750 мм; W1=700 мм; Weight=31.50 кг; Width=750 мм; d=12 мм; l=200 мм; l1=-200 мм; n=12; r1=345 мм
- Axis-FP-630-4D/0,55-8/30/AL: D1=690 мм; D2=730 мм; Diameter=630 мм; Dn=634 мм; Dv=620 мм; Dy=630 мм; Height=400 мм; L=400 мм; Ld=120 мм; Length=730 мм; Lv=105 мм; Maximum Air Flow=8280.0 м³/ч; Motor=Motor : 0.55 kW; N=8; P=355 мм; Power=550 Вт; W=750 мм; W1=700 мм; Weight=31.50 кг; Width=750 мм; d=12 мм; l=200 мм; l1=-200 мм; n=12; r1=345 мм
- Axis-FP-630-4D/0,75-8/35/AL: D1=690 мм; D2=730 мм; Diameter=630 мм; Dn=634 мм; Dv=620 мм; Dy=630 мм; Height=400 мм; L=400 мм; Ld=120 мм; Length=730 мм; Lv=105 мм; Maximum Air Flow=10260.0 м³/ч; Motor=Motor : 0.75 kW; N=8; P=355 мм; Power=750 Вт; W=750 мм; W1=700 мм; Weight=32.50 кг; Width=750 мм; d=12 мм; l=200 мм; l1=-200 мм; n=12; r1=345 мм
- Axis-FP-630-4D/1,1-8/40/AL: D1=690 мм; D2=730 мм; Diameter=630 мм; Dn=634 мм; Dv=620 мм; Dy=630 мм; Height=400 мм; L=400 мм; Ld=120 мм; Length=730 мм; Lv=105 мм; Maximum Air Flow=11520.0 м³/ч; Motor=Motor : 1.1 kW; N=8; P=355 мм; Power=1100 Вт; W=750 мм; W1=700 мм; Weight=36.50 кг; Width=750 мм; d=12 мм; l=200 мм; l1=-200 мм; n=12; r1=345 мм
- Axis-FP-630-4D/1,1-6/32,5/AL: D1=690 мм; D2=730 мм; Diameter=630 мм; Dn=634 мм; Dv=620 мм; Dy=630 мм; Height=400 мм; L=400 мм; Ld=120 мм; Length=730 мм; Lv=105 мм; Maximum Air Flow=12780.0 м³/ч; Motor=Motor : 1.1 kW; N=6; P=355 мм; Power=1100 Вт; W=750 мм; W1=700 мм; Weight=38.50 кг; Width=750 мм; d=12 мм; l=200 мм; l1=-200 мм; n=12; r1=345 мм
- Axis-FP-630-4D/1,5-6/37,5/AL: D1=690 мм; D2=730 мм; Diameter=630 мм; Dn=634 мм; Dv=620 мм; Dy=630 мм; Height=400 мм; L=400 мм; Ld=120 мм; Length=730 мм; Lv=105 мм; Maximum Air Flow=14040.0 м³/ч; Motor=Motor : 1.5kW; N=6; P=355 мм; Power=1500 Вт; W=750 мм; W1=700 мм; Weight=42.50 кг; Width=750 мм; d=12 мм; l=200 мм; l1=-200 мм; n=12; r1=345 мм
- Axis-FP-630-4D/2,2-6/45/AL: D1=690 мм; D2=730 мм; Diameter=630 мм; Dn=634 мм; Dv=620 мм; Dy=630 мм; Height=400 мм; L=400 мм; Ld=120 мм; Length=730 мм; Lv=105 мм; Maximum Air Flow=15660.0 м³/ч; Motor=Motor : 2.2kW; N=6; P=355 мм; Power=2200 Вт; W=750 мм; W1=700 мм; Weight=48.50 кг; Width=750 мм; d=12 мм; l=200 мм; l1=-200 мм; n=12; r1=345 мм
- Axis-FP-630-2/4D/2,2/0,5-6/25/AL: D1=690 мм; D2=730 мм; Diameter=630 мм; Dn=634 мм; Dv=620 мм; Dy=630 мм; Height=400 мм; L=400 мм; Ld=120 мм; Length=730 мм; Lv=105 мм; Maximum Air Flow=13860.0 м³/ч; Motor=Motor : 2.2kW; N=6; P=355 мм; Power=2200 Вт; W=750 мм; W1=700 мм; Weight=46.50 кг; Width=750 мм; d=12 мм; l=200 мм; l1=-200 мм; n=12; r1=345 мм
- Axis-FP-630-2/4D/3,1/0,8-6/30/AL: D1=690 мм; D2=730 мм; Diameter=630 мм; Dn=634 мм; Dv=620 мм; Dy=630 мм; Height=500 мм; L=500 мм; Ld=150 мм; Length=730 мм; Lv=135 мм; Maximum Air Flow=16920.0 м³/ч; Motor=Motor : 3.1 kW; N=6; P=355 мм; Power=3100 Вт; W=750 мм; W1=700 мм; Weight=60.00 кг; Width=750 мм; d=12 мм; l=250 мм; l1=-250 мм; n=12; r1=345 мм
- Axis-FP-630-2/4D/4,4/1,1-7/32,5/AL: D1=690 мм; D2=730 мм; Diameter=630 мм; Dn=634 мм; Dv=620 мм; Dy=630 мм; Height=500 мм; L=500 мм; Ld=150 мм; Length=730 мм; Lv=135 мм; Maximum Air Flow=18540.0 м³/ч; Motor=Motor : 4.4 kW; N=7; P=355 мм; Power=4400 Вт; W=750 мм; W1=700 мм; Weight=72.50 кг; Width=750 мм; d=12 мм; l=250 мм; l1=-250 мм; n=12; r1=345 мм
- Axis-FP-630-2/4D/6/1,5-7/35/AL: D1=690 мм; D2=730 мм; Diameter=630 мм; Dn=634 мм; Dv=620 мм; Dy=630 мм; Height=550 мм; L=550 мм; Ld=165 мм; Length=730 мм; Lv=150 мм; Maximum Air Flow=21060.0 м³/ч; Motor=Motor : 6 kW; N=7; P=355 мм; Power=6000 Вт; W=750 мм; W1=700 мм; Weight=102.00 кг; Width=750 мм; d=12 мм; l=275 мм; l1=-275 мм; n=12; r1=345 мм
- Axis-FP-630-2/4D/6/1,5-7/37,5/AL: D1=690 мм; D2=730 мм; Diameter=630 мм; Dn=634 мм; Dv=620 мм; Dy=630 мм; Height=550 мм; L=550 мм; Ld=165 мм; Length=730 мм; Lv=150 мм; Maximum Air Flow=21960.0 м³/ч; Motor=Motor : 6 kW; N=7; P=355 мм; Power=6000 Вт; W=750 мм; W1=700 мм; Weight=102.00 кг; Width=750 мм; d=12 мм; l=275 мм; l1=-275 мм; n=12; r1=345 мм
- Axis-FP-630-2/4D/8/2-7/41,5/AL: D1=690 мм; D2=730 мм; Diameter=630 мм; Dn=634 мм; Dv=620 мм; Dy=630 мм; Height=550 мм; L=550 мм; Ld=165 мм; Length=730 мм; Lv=150 мм; Maximum Air Flow=24120.0 м³/ч; Motor=Motor : 8 кВт; N=7; P=355 мм; Power=8000 Вт; W=750 мм; W1=700 мм; Weight=111.00 кг; Width=750 мм; d=12 мм; l=275 мм; l1=-275 мм; n=12; r1=345 мм
- Axis-FP-630-2/4D/12/3-8/41,5/AL: D1=690 мм; D2=730 мм; Diameter=630 мм; Dn=634 мм; Dv=620 мм; Dy=630 мм; Height=700 мм; L=700 мм; Ld=210 мм; Length=730 мм; Lv=195 мм; Maximum Air Flow=26100.0 м³/ч; Motor=Motor : 12 kW; N=8; P=355 мм; Power=12000 Вт; W=750 мм; W1=700 мм; Weight=177.00 кг; Width=750 мм; d=12 мм; l=350 мм; l1=-350 мм; n=12; r1=345 мм
- Axis-FP-630-2/4D/16/4-8/46,5/AL: D1=690 мм; D2=730 мм; Diameter=630 мм; Dn=634 мм; Dv=620 мм; Dy=630 мм; Height=700 мм; L=700 мм; Ld=210 мм; Length=730 мм; Lv=195 мм; Maximum Air Flow=28080.0 м³/ч; Motor=Motor : 16 kW; N=8; P=355 мм; Power=16000 Вт; W=750 мм; W1=700 мм; Weight=194.00 кг; Width=750 мм; d=12 мм; l=350 мм; l1=-350 мм; n=12; r1=345 мм
- Axis-FP-630-2/4D/16/4-9/48,5/AL: D1=690 мм; D2=730 мм; Diameter=630 мм; Dn=634 мм; Dv=620 мм; Dy=630 мм; Height=700 мм; L=700 мм; Ld=210 мм; Length=730 мм; Lv=195 мм; Maximum Air Flow=30060.0 м³/ч; Motor=Motor : 16 kW; N=9; P=355 мм; Power=16000 Вт; W=750 мм; W1=700 мм; Weight=195.00 кг; Width=750 мм; d=12 мм; l=350 мм; l1=-350 мм; n=12; r1=345 мм
- Axis-FP-630-4/6D/0,55/0,2-8/25/AL: D1=690 мм; D2=730 мм; Diameter=630 мм; Dn=634 мм; Dv=620 мм; Dy=630 мм; Height=400 мм; L=400 мм; Ld=120 мм; Length=730 мм; Lv=105 мм; Maximum Air Flow=6480.0 м³/ч; Motor=Motor : 0.55 kW; N=8; P=355 мм; Power=5500 Вт; W=750 мм; W1=700 мм; Weight=34.00 кг; Width=750 мм; d=12 мм; l=200 мм; l1=-200 мм; n=12; r1=345 мм
- Axis-FP-630-4/6D/0,55/0,2-8/30/AL: D1=690 мм; D2=730 мм; Diameter=630 мм; Dn=634 мм; Dv=620 мм; Dy=630 мм; Height=400 мм; L=400 мм; Ld=120 мм; Length=730 мм; Lv=105 мм; Maximum Air Flow=7920.0 м³/ч; Motor=Motor : 0.55 kW; N=8; P=355 мм; Power=5500 Вт; W=750 мм; W1=700 мм; Weight=34.00 кг; Width=750 мм; d=12 мм; l=200 мм; l1=-200 мм; n=12; r1=345 мм
- Axis-FP-630-4/6D/0,75/0,25-8/35/AL: D1=690 мм; D2=730 мм; Diameter=630 мм; Dn=634 мм; Dv=620 мм; Dy=630 мм; Height=400 мм; L=400 мм; Ld=120 мм; Length=730 мм; Lv=105 мм; Maximum Air Flow=10080.0 м³/ч; Motor=Motor : 0.75 kW; N=8; P=355 мм; Power=7500 Вт; W=750 мм; W1=700 мм; Weight=34.00 кг; Width=750 мм; d=12 мм; l=200 мм; l1=-200 мм; n=12; r1=345 мм
- Axis-FP-630-4/6D/1,1/0,3-8/40/AL: D1=690 мм; D2=730 мм; Diameter=630 мм; Dn=634 мм; Dv=620 мм; Dy=630 мм; Height=400 мм; L=400 мм; Ld=120 мм; Length=730 мм; Lv=105 мм; Maximum Air Flow=11520.0 м³/ч; Motor=Motor : 1.1 kW; N=8; P=355 мм; Power=1100 Вт; W=750 мм; W1=700 мм; Weight=39.50 кг; Width=750 мм; d=12 мм; l=200 мм; l1=-200 мм; n=12; r1=345 мм
- Axis-FP-630-4/6D/1,1/0,3-6/32,5/AL: D1=690 мм; D2=730 мм; Diameter=630 мм; Dn=634 мм; Dv=620 мм; Dy=630 мм; Height=400 мм; L=400 мм; Ld=120 мм; Length=730 мм; Lv=105 мм; Maximum Air Flow=12960.0 м³/ч; Motor=Motor : 1.1 kW; N=6; P=355 мм; Power=1100 Вт; W=750 мм; W1=700 мм; Weight=42.00 кг; Width=750 мм; d=12 мм; l=200 мм; l1=-200 мм; n=12; r1=345 мм
- Axis-FP-630-4/6D/1,5/0,37-6/37,5/AL: D1=690 мм; D2=730 мм; Diameter=630 мм; Dn=634 мм; Dv=620 мм; Dy=630 мм; Height=400 мм; L=400 мм; Ld=120 мм; Length=730 мм; Lv=105 мм; Maximum Air Flow=13860.0 м³/ч; Motor=Motor : 1.5kW; N=6; P=355 мм; Power=1500 Вт; W=750 мм; W1=700 мм; Weight=46.00 кг; Width=750 мм; d=12 мм; l=200 мм; l1=-200 мм; n=12; r1=345 мм
- Axis-FP-630-4/6D/2,2/0,7-6/45/AL: D1=690 мм; D2=730 мм; Diameter=630 мм; Dn=634 мм; Dv=620 мм; Dy=630 мм; Height=500 мм; L=500 мм; Ld=150 мм; Length=730 мм; Lv=135 мм; Maximum Air Flow=15660.0 м³/ч; Motor=Motor : 2.2kW; N=6; P=355 мм; Power=2200 Вт; W=750 мм; W1=700 мм; Weight=57.00 кг; Width=750 мм; d=12 мм; l=250 мм; l1=-250 мм; n=12; r1=345 мм
- Axis-FP-630-4/8D/0,6/0,15-8/25/AL: D1=690 мм; D2=730 мм; Diameter=630 мм; Dn=634 мм; Dv=620 мм; Dy=630 мм; Height=400 мм; L=400 мм; Ld=120 мм; Length=730 мм; Lv=105 мм; Maximum Air Flow=6480.0 м³/ч; Motor=Motor : 0.55 kW; N=8; P=355 мм; Power=600 Вт; W=750 мм; W1=700 мм; Weight=38.00 кг; Width=750 мм; d=12 мм; l=200 мм; l1=-200 мм; n=12; r1=345 мм
- Axis-FP-630-4/8D/0,6/0,15-8/30/AL: D1=690 мм; D2=730 мм; Diameter=630 мм; Dn=634 мм; Dv=620 мм; Dy=630 мм; Height=400 мм; L=400 мм; Ld=120 мм; Length=730 мм; Lv=105 мм; Maximum Air Flow=7920.0 м³/ч; Motor=Motor : 0.55 kW; N=8; P=355 мм; Power=600 Вт; W=750 мм; W1=700 мм; Weight=38.00 кг; Width=750 мм; d=12 мм; l=200 мм; l1=-200 мм; n=12; r1=345 мм
- Axis-FP-630-4/8D/0,8/0,2-8/35/AL: D1=690 мм; D2=730 мм; Diameter=630 мм; Dn=634 мм; Dv=620 мм; Dy=630 мм; Height=400 мм; L=400 мм; Ld=120 мм; Length=730 мм; Lv=105 мм; Maximum Air Flow=10080.0 м³/ч; Motor=Motor : 0.75 kW; N=8; P=355 мм; Power=800 Вт; W=750 мм; W1=700 мм; Weight=38.00 кг; Width=750 мм; d=12 мм; l=200 мм; l1=-200 мм; n=12; r1=345 мм
- Axis-FP-630-4/8D/1,2/0,3-8/40/AL: D1=690 мм; D2=730 мм; Diameter=630 мм; Dn=634 мм; Dv=620 мм; Dy=630 мм; Height=400 мм; L=400 мм; Ld=120 мм; Length=730 мм; Lv=105 мм; Maximum Air Flow=11520.0 м³/ч; Motor=Motor : 1.1 kW; N=8; P=355 мм; Power=1200 Вт; W=750 мм; W1=700 мм; Weight=43.50 кг; Width=750 мм; d=12 мм; l=200 мм; l1=-200 мм; n=12; r1=345 мм
- Axis-FP-630-4/8D/1,2/0,3-6/32,5/AL: D1=690 мм; D2=730 мм; Diameter=630 мм; Dn=634 мм; Dv=620 мм; Dy=630 мм; Height=400 мм; L=400 мм; Ld=120 мм; Length=730 мм; Lv=105 мм; Maximum Air Flow=12960.0 м³/ч; Motor=Motor : 1.1 kW; N=6; P=355 мм; Power=1200 Вт; W=750 мм; W1=700 мм; Weight=46.00 кг; Width=750 мм; d=12 мм; l=200 мм; l1=-200 мм; n=12; r1=345 мм
- Axis-FP-630-4/8D/1,6/0,4-6/37,5/AL: D1=690 мм; D2=730 мм; Diameter=630 мм; Dn=634 мм; Dv=620 мм; Dy=630 мм; Height=400 мм; L=400 мм; Ld=120 мм; Length=730 мм; Lv=105 мм; Maximum Air Flow=14040.0 м³/ч; Motor=Motor : 1.5kW; N=6; P=355 мм; Power=1600 Вт; W=750 мм; W1=700 мм; Weight=49.00 кг; Width=750 мм; d=12 мм; l=200 мм; l1=-200 мм; n=12; r1=345 мм
- Axis-FP-630-4/8D/2,2/0,55-6/45/AL: D1=690 мм; D2=730 мм; Diameter=630 мм; Dn=634 мм; Dv=620 мм; Dy=630 мм; Height=500 мм; L=500 мм; Ld=150 мм; Length=730 мм; Lv=135 мм; Maximum Air Flow=15660.0 м³/ч; Motor=Motor : 2.2kW; N=6; P=355 мм; Power=2200 Вт; W=750 мм; W1=700 мм; Weight=60.00 кг; Width=750 мм; d=12 мм; l=250 мм; l1=-250 мм; n=12; r1=345 мм
- Axis-FP-710-4D/1,1-6/25/AL: D1=770 мм; D2=810 мм; Diameter=710 мм; Dn=714 мм; Dv=700 мм; Dy=710 мм; Height=400 мм; L=400 мм; Ld=120 мм; Length=810 мм; Lv=105 мм; Maximum Air Flow=14040.0 м³/ч; Motor=Motor : 1.1 kW; N=6; P=395 мм; Power=1100 Вт; W=845 мм; W1=795 мм; Weight=51.50 кг; Width=845 мм; d=12 мм; l=200 мм; l1=-200 мм; n=16; r1=385 мм
- Axis-FP-710-4D/1,5-6/30/AL: D1=770 мм; D2=810 мм; Diameter=710 мм; Dn=714 мм; Dv=700 мм; Dy=710 мм; Height=400 мм; L=400 мм; Ld=120 мм; Length=810 мм; Lv=105 мм; Maximum Air Flow=16380.0 м³/ч; Motor=Motor : 1.5kW; N=6; P=395 мм; Power=1500 Вт; W=845 мм; W1=795 мм; Weight=55.00 кг; Width=845 мм; d=12 мм; l=200 мм; l1=-200 мм; n=16; r1=385 мм
- Axis-FP-710-4D/2,2-6/35/AL: D1=770 мм; D2=810 мм; Diameter=710 мм; Dn=714 мм; Dv=700 мм; Dy=710 мм; Height=400 мм; L=400 мм; Ld=120 мм; Length=810 мм; Lv=105 мм; Maximum Air Flow=18900.0 м³/ч; Motor=Motor : 2.2kW; N=6; P=395 мм; Power=2200 Вт; W=845 мм; W1=795 мм; Weight=61.00 кг; Width=845 мм; d=12 мм; l=200 мм; l1=-200 мм; n=16; r1=385 мм
- Axis-FP-710-4D/2,2-6/40/AL: D1=770 мм; D2=810 мм; Diameter=710 мм; Dn=714 мм; Dv=700 мм; Dy=710 мм; Height=400 мм; L=400 мм; Ld=120 мм; Length=810 мм; Lv=105 мм; Maximum Air Flow=19800.0 м³/ч; Motor=Motor : 2.2kW; N=6; P=395 мм; Power=2200 Вт; W=845 мм; W1=795 мм; Weight=61.00 кг; Width=845 мм; d=12 мм; l=200 мм; l1=-200 мм; n=16; r1=385 мм
- Axis-FP-710-4D/3-6/45/AL: D1=770 мм; D2=810 мм; Diameter=710 мм; Dn=714 мм; Dv=700 мм; Dy=710 мм; Height=500 мм; L=500 мм; Ld=150 мм; Length=810 мм; Lv=135 мм; Maximum Air Flow=21960.0 м³/ч; Motor=Motor : 3 kW; N=6; P=395 мм; Power=3000 Вт; W=845 мм; W1=795 мм; Weight=75.00 кг; Width=845 мм; d=12 мм; l=250 мм; l1=-250 мм; n=16; r1=385 мм
- Axis-FP-710-6D/0,25-6/20/AL: D1=770 мм; D2=810 мм; Diameter=710 мм; Dn=714 мм; Dv=700 мм; Dy=710 мм; Height=400 мм; L=400 мм; Ld=120 мм; Length=810 мм; Lv=105 мм; Maximum Air Flow=7200.0 м³/ч; Motor=Motor : 0.25 kW; N=6; P=395 мм; Power=250 Вт; W=845 мм; W1=795 мм; Weight=45.50 кг; Width=845 мм; d=12 мм; l=200 мм; l1=-200 мм; n=16; r1=385 мм
- Axis-FP-710-6D/0,25-6/25/AL: D1=770 мм; D2=810 мм; Diameter=710 мм; Dn=714 мм; Dv=700 мм; Dy=710 мм; Height=400 мм; L=400 мм; Ld=120 мм; Length=810 мм; Lv=105 мм; Maximum Air Flow=9000.0 м³/ч; Motor=Motor : 0.25 kW; N=6; P=395 мм; Power=250 Вт; W=845 мм; W1=795 мм; Weight=45.50 кг; Width=845 мм; d=12 мм; l=200 мм; l1=-200 мм; n=16; r1=385 мм
- Axis-FP-710-6D/0,37-6/30/AL: D1=770 мм; D2=810 мм; Diameter=710 мм; Dn=714 мм; Dv=700 мм; Dy=710 мм; Height=400 мм; L=400 мм; Ld=120 мм; Length=810 мм; Lv=105 мм; Maximum Air Flow=10800.0 м³/ч; Motor=Motor : 0.37 kW; N=6; P=395 мм; Power=370 Вт; W=845 мм; W1=795 мм; Weight=49.50 кг; Width=845 мм; d=12 мм; l=200 мм; l1=-200 мм; n=16; r1=385 мм
- Axis-FP-710-6D/0,55-6/35/AL: D1=770 мм; D2=810 мм; Diameter=710 мм; Dn=714 мм; Dv=700 мм; Dy=710 мм; Height=400 мм; L=400 мм; Ld=120 мм; Length=810 мм; Lv=105 мм; Maximum Air Flow=12600.0 м³/ч; Motor=Motor : 0.55 kW; N=6; P=395 мм; Power=550 Вт; W=845 мм; W1=795 мм; Weight=53.00 кг; Width=845 мм; d=12 мм; l=200 мм; l1=-200 мм; n=16; r1=385 мм
- Axis-FP-710-6D/0,75-6/40/AL: D1=770 мм; D2=810 мм; Diameter=710 мм; Dn=714 мм; Dv=700 мм; Dy=710 мм; Height=400 мм; L=400 мм; Ld=120 мм; Length=810 мм; Lv=105 мм; Maximum Air Flow=13140.0 м³/ч; Motor=Motor : 0.75 kW; N=6; P=395 мм; Power=750 Вт; W=845 мм; W1=795 мм; Weight=56.00 кг; Width=845 мм; d=12 мм; l=200 мм; l1=-200 мм; n=16; r1=385 мм
- Axis-FP-710-6D/1,1-6/45/AL: D1=770 мм; D2=810 мм; Diameter=710 мм; Dn=714 мм; Dv=700 мм; Dy=710 мм; Height=400 мм; L=400 мм; Ld=120 мм; Length=810 мм; Lv=105 мм; Maximum Air Flow=14580.0 м³/ч; Motor=Motor : 1.1 kW; N=6; P=395 мм; Power=1100 Вт; W=845 мм; W1=795 мм; Weight=60.00 кг; Width=845 мм; d=12 мм; l=200 мм; l1=-200 мм; n=16; r1=385 мм
- Axis-FP-710-4/6D/0,75/0,25-6/20/AL: D1=770 мм; D2=810 мм; Diameter=710 мм; Dn=714 мм; Dv=700 мм; Dy=710 мм; Height=400 мм; L=400 мм; Ld=120 мм; Length=810 мм; Lv=105 мм; Maximum Air Flow=10800.0 м³/ч; Motor=Motor : 0.75 kW; N=6; P=395 мм; Power=750 Вт; W=845 мм; W1=795 мм; Weight=49.00 кг; Width=845 мм; d=12 мм; l=200 мм; l1=-200 мм; n=16; r1=385 мм
- Axis-FP-710-4/6D/1,1/0,3-6/25/AL: D1=770 мм; D2=810 мм; Diameter=710 мм; Dn=714 мм; Dv=700 мм; Dy=710 мм; Height=400 мм; L=400 мм; Ld=120 мм; Length=810 мм; Lv=105 мм; Maximum Air Flow=13500.0 м³/ч; Motor=Motor : 1.1 kW; N=6; P=395 мм; Power=1100 Вт; W=845 мм; W1=795 мм; Weight=54.00 кг; Width=845 мм; d=12 мм; l=200 мм; l1=-200 мм; n=16; r1=385 мм
- Axis-FP-710-4/6D/1,5/0,37-6/30/AL: D1=770 мм; D2=810 мм; Diameter=710 мм; Dn=714 мм; Dv=700 мм; Dy=710 мм; Height=400 мм; L=400 мм; Ld=120 мм; Length=810 мм; Lv=105 мм; Maximum Air Flow=16380.0 м³/ч; Motor=Motor : 1.5kW; N=6; P=395 мм; Power=1500 Вт; W=845 мм; W1=795 мм; Weight=58.00 кг; Width=845 мм; d=12 мм; l=200 мм; l1=-200 мм; n=16; r1=385 мм
- Axis-FP-710-4/6D/2,2/0,7-6/35/AL: D1=770 мм; D2=810 мм; Diameter=710 мм; Dn=714 мм; Dv=700 мм; Dy=710 мм; Height=500 мм; L=500 мм; Ld=150 мм; Length=810 мм; Lv=135 мм; Maximum Air Flow=18540.0 м³/ч; Motor=Motor : 2.2kW; N=6; P=395 мм; Power=2200 Вт; W=845 мм; W1=795 мм; Weight=72.00 кг; Width=845 мм; d=12 мм; l=250 мм; l1=-250 мм; n=16; r1=385 мм
- Axis-FP-710-4/6D/2,2/0,7-6/40/AL: D1=770 мм; D2=810 мм; Diameter=710 мм; Dn=714 мм; Dv=700 мм; Dy=710 мм; Height=500 мм; L=500 мм; Ld=150 мм; Length=810 мм; Lv=135 мм; Maximum Air Flow=19620.0 м³/ч; Motor=Motor : 2.2kW; N=6; P=395 мм; Power=2200 Вт; W=845 мм; W1=795 мм; Weight=72.00 кг; Width=845 мм; d=12 мм; l=250 мм; l1=-250 мм; n=16; r1=385 мм
- Axis-FP-710-4/6D/3/1-6/45/AL: D1=770 мм; D2=810 мм; Diameter=710 мм; Dn=714 мм; Dv=700 мм; Dy=710 мм; Height=500 мм; L=500 мм; Ld=150 мм; Length=810 мм; Lv=135 мм; Maximum Air Flow=21780.0 м³/ч; Motor=Motor : 3 kW; N=6; P=395 мм; Power=3000 Вт; W=845 мм; W1=795 мм; Weight=81.00 кг; Width=845 мм; d=12 мм; l=250 мм; l1=-250 мм; n=16; r1=385 мм
- Axis-FP-710-4/8D/0,8/0,2-6/20/AL: D1=770 мм; D2=810 мм; Diameter=710 мм; Dn=714 мм; Dv=700 мм; Dy=710 мм; Height=400 мм; L=400 мм; Ld=120 мм; Length=810 мм; Lv=105 мм; Maximum Air Flow=10800.0 м³/ч; Motor=Motor : 0.8 kW; N=6; P=395 мм; Power=800 Вт; W=845 мм; W1=795 мм; Weight=52.00 кг; Width=845 мм; d=12 мм; l=200 мм; l1=-200 мм; n=16; r1=385 мм
- Axis-FP-710-4/8D/1,2/0,3-6/25/AL: D1=770 мм; D2=810 мм; Diameter=710 мм; Dn=714 мм; Dv=700 мм; Dy=710 мм; Height=400 мм; L=400 мм; Ld=120 мм; Length=810 мм; Lv=105 мм; Maximum Air Flow=13680.0 м³/ч; Motor=Motor : 1.1 kW; N=6; P=395 мм; Power=1200 Вт; W=845 мм; W1=795 мм; Weight=58.00 кг; Width=845 мм; d=12 мм; l=200 мм; l1=-200 мм; n=16; r1=385 мм
- Axis-FP-710-4/8D/1,6/0,4-6/30/AL: D1=770 мм; D2=810 мм; Diameter=710 мм; Dn=714 мм; Dv=700 мм; Dy=710 мм; Height=400 мм; L=400 мм; Ld=120 мм; Length=810 мм; Lv=105 мм; Maximum Air Flow=16380.0 м³/ч; Motor=Motor : 1.5kW; N=6; P=395 мм; Power=1600 Вт; W=845 мм; W1=795 мм; Weight=61.00 кг; Width=845 мм; d=12 мм; l=200 мм; l1=-200 мм; n=16; r1=385 мм
- Axis-FP-710-4/8D/2,2/0,55-6/35/AL: D1=770 мм; D2=810 мм; Diameter=710 мм; Dn=714 мм; Dv=700 мм; Dy=710 мм; Height=500 мм; L=500 мм; Ld=150 мм; Length=810 мм; Lv=135 мм; Maximum Air Flow=18540.0 м³/ч; Motor=Motor : 2.2kW; N=6; P=395 мм; Power=2200 Вт; W=845 мм; W1=795 мм; Weight=75.00 кг; Width=845 мм; d=12 мм; l=250 мм; l1=-250 мм; n=16; r1=385 мм
- Axis-FP-710-4/8D/2,2/0,55-6/40/AL: D1=770 мм; D2=810 мм; Diameter=710 мм; Dn=714 мм; Dv=700 мм; Dy=710 мм; Height=500 мм; L=500 мм; Ld=150 мм; Length=810 мм; Lv=135 мм; Maximum Air Flow=19800.0 м³/ч; Motor=Motor : 2.2kW; N=6; P=395 мм; Power=2200 Вт; W=845 мм; W1=795 мм; Weight=75.00 кг; Width=845 мм; d=12 мм; l=250 мм; l1=-250 мм; n=16; r1=385 мм
- Axis-FP-710-4/8D/2,8/0,7-6/45/AL: D1=770 мм; D2=810 мм; Diameter=710 мм; Dn=714 мм; Dv=700 мм; Dy=710 мм; Height=500 мм; L=500 мм; Ld=150 мм; Length=810 мм; Lv=135 мм; Maximum Air Flow=21780.0 м³/ч; Motor=Motor : 2.8 kW; N=6; P=395 мм; Power=2800 Вт; W=845 мм; W1=795 мм; Weight=78.00 кг; Width=845 мм; d=12 мм; l=250 мм; l1=-250 мм; n=16; r1=385 мм
- Axis-FP-800-4D/1,5-6/25/AL: D1=860 мм; D2=900 мм; Diameter=800 мм; Dn=804 мм; Dv=790 мм; Dy=800 мм; Height=400 мм; L=400 мм; Ld=120 мм; Length=900 мм; Lv=105 мм; Maximum Air Flow=18000.0 м³/ч; Motor=Motor : 1.5kW; N=6; P=440 мм; Power=1500 Вт; W=925 мм; W1=875 мм; Weight=65.50 кг; Width=925 мм; d=12 мм; l=200 мм; l1=-200 мм; n=16; r1=430 мм
- Axis-FP-800-4D/2,2-6/30/AL: D1=860 мм; D2=900 мм; Diameter=800 мм; Dn=804 мм; Dv=790 мм; Dy=800 мм; Height=400 мм; L=400 мм; Ld=120 мм; Length=900 мм; Lv=105 мм; Maximum Air Flow=21060.0 м³/ч; Motor=Motor : 2.2kW; N=6; P=440 мм; Power=2200 Вт; W=925 мм; W1=875 мм; Weight=65.50 кг; Width=925 мм; d=12 мм; l=200 мм; l1=-200 мм; n=16; r1=430 мм
- Axis-FP-800-4D/3-6/32,5/AL: D1=860 мм; D2=900 мм; Diameter=800 мм; Dn=804 мм; Dv=790 мм; Dy=800 мм; Height=500 мм; L=500 мм; Ld=150 мм; Length=900 мм; Lv=135 мм; Maximum Air Flow=23040.0 м³/ч; Motor=Motor : 3 kW; N=6; P=440 мм; Power=3000 Вт; W=925 мм; W1=875 мм; Weight=80.00 кг; Width=925 мм; d=12 мм; l=250 мм; l1=-250 мм; n=16; r1=430 мм
- Axis-FP-800-4D/3-6/35/AL: D1=860 мм; D2=900 мм; Diameter=800 мм; Dn=804 мм; Dv=790 мм; Dy=800 мм; Height=500 мм; L=500 мм; Ld=150 мм; Length=900 мм; Lv=135 мм; Maximum Air Flow=25200.0 м³/ч; Motor=Motor : 3 kW; N=6; P=440 мм; Power=3000 Вт; W=925 мм; W1=875 мм; Weight=80.00 кг; Width=925 мм; d=12 мм; l=250 мм; l1=-250 мм; n=16; r1=430 мм
- Axis-FP-800-4D/4-6/37,5/AL: D1=860 мм; D2=900 мм; Diameter=800 мм; Dn=804 мм; Dv=790 мм; Dy=800 мм; Height=500 мм; L=500 мм; Ld=150 мм; Length=900 мм; Lv=135 мм; Maximum Air Flow=26100.0 м³/ч; Motor=Motor : 4 kW; N=6; P=440 мм; Power=4000 Вт; W=925 мм; W1=875 мм; Weight=85.00 кг; Width=925 мм; d=12 мм; l=250 мм; l1=-250 мм; n=16; r1=430 мм
- Axis-FP-800-4D/4-6/40/AL: D1=860 мм; D2=900 мм; Diameter=800 мм; Dn=804 мм; Dv=790 мм; Dy=800 мм; Height=500 мм; L=500 мм; Ld=150 мм; Length=900 мм; Lv=135 мм; Maximum Air Flow=27000.0 м³/ч; Motor=Motor : 4 kW; N=6; P=440 мм; Power=4000 Вт; W=925 мм; W1=875 мм; Weight=85.00 кг; Width=925 мм; d=12 мм; l=250 мм; l1=-250 мм; n=16; r1=430 мм
- Axis-FP-800-4D/5,5-6/45/AL: D1=860 мм; D2=900 мм; Diameter=800 мм; Dn=804 мм; Dv=790 мм; Dy=800 мм; Height=550 мм; L=550 мм; Ld=165 мм; Length=900 мм; Lv=150 мм; Maximum Air Flow=28800.0 м³/ч; Motor=Motor : 5.5 kW; N=6; P=440 мм; Power=5500 Вт; W=925 мм; W1=875 мм; Weight=104.00 кг; Width=925 мм; d=12 мм; l=275 мм; l1=-275 мм; n=16; r1=430 мм
- Axis-FP-800-6D/0,37-6/20/AL: D1=860 мм; D2=900 мм; Diameter=800 мм; Dn=804 мм; Dv=790 мм; Dy=800 мм; Height=400 мм; L=400 мм; Ld=120 мм; Length=900 мм; Lv=105 мм; Maximum Air Flow=9000.0 м³/ч; Motor=Motor : 0.37 kW; N=6; P=440 мм; Power=370 Вт; W=925 мм; W1=875 мм; Weight=53.50 кг; Width=925 мм; d=12 мм; l=200 мм; l1=-200 мм; n=16; r1=430 мм
- Axis-FP-800-6D/0,55-6/25/AL: D1=860 мм; D2=900 мм; Diameter=800 мм; Dn=804 мм; Dv=790 мм; Dy=800 мм; Height=400 мм; L=400 мм; Ld=120 мм; Length=900 мм; Lv=105 мм; Maximum Air Flow=11880.0 м³/ч; Motor=Motor : 0.55 kW; N=6; P=440 мм; Power=550 Вт; W=925 мм; W1=875 мм; Weight=56.50 кг; Width=925 мм; d=12 мм; l=200 мм; l1=-200 мм; n=16; r1=430 мм
- Axis-FP-800-6D/0,75-6/30/AL: D1=860 мм; D2=900 мм; Diameter=800 мм; Dn=804 мм; Dv=790 мм; Dy=800 мм; Height=400 мм; L=400 мм; Ld=120 мм; Length=900 мм; Lv=105 мм; Maximum Air Flow=14040.0 м³/ч; Motor=Motor : 0.75 kW; N=6; P=440 мм; Power=750 Вт; W=925 мм; W1=875 мм; Weight=60.50 кг; Width=925 мм; d=12 мм; l=200 мм; l1=-200 мм; n=16; r1=430 мм
- Axis-FP-800-6D/0,75-6/32,5/AL: D1=860 мм; D2=900 мм; Diameter=800 мм; Dn=804 мм; Dv=790 мм; Dy=800 мм; Height=400 мм; L=400 мм; Ld=120 мм; Length=900 мм; Lv=105 мм; Maximum Air Flow=15480.0 м³/ч; Motor=Motor : 0.75 kW; N=6; P=440 мм; Power=750 Вт; W=925 мм; W1=875 мм; Weight=60.50 кг; Width=925 мм; d=12 мм; l=200 мм; l1=-200 мм; n=16; r1=430 мм
- Axis-FP-800-6D/1,1-6/35/AL: D1=860 мм; D2=900 мм; Diameter=800 мм; Dn=804 мм; Dv=790 мм; Dy=800 мм; Height=400 мм; L=400 мм; Ld=120 мм; Length=900 мм; Lv=105 мм; Maximum Air Flow=15840.0 м³/ч; Motor=Motor : 1.1 kW; N=6; P=440 мм; Power=1100 Вт; W=925 мм; W1=875 мм; Weight=64.50 кг; Width=925 мм; d=12 мм; l=200 мм; l1=-200 мм; n=16; r1=430 мм
- Axis-FP-800-6D/1,1-6/37,5/AL: D1=860 мм; D2=900 мм; Diameter=800 мм; Dn=804 мм; Dv=790 мм; Dy=800 мм; Height=400 мм; L=400 мм; Ld=120 мм; Length=900 мм; Lv=105 мм; Maximum Air Flow=16920.0 м³/ч; Motor=Motor : 1.1 kW; N=6; P=440 мм; Power=1100 Вт; W=925 мм; W1=875 мм; Weight=64.50 кг; Width=925 мм; d=12 мм; l=200 мм; l1=-200 мм; n=16; r1=430 мм
- Axis-FP-800-6D/1,1-6/40/AL: D1=860 мм; D2=900 мм; Diameter=800 мм; Dn=804 мм; Dv=790 мм; Dy=800 мм; Height=400 мм; L=400 мм; Ld=120 мм; Length=900 мм; Lv=105 мм; Maximum Air Flow=18000.0 м³/ч; Motor=Motor : 1.1 kW; N=6; P=440 мм; Power=1100 Вт; W=925 мм; W1=875 мм; Weight=64.50 кг; Width=925 мм; d=12 мм; l=200 мм; l1=-200 мм; n=16; r1=430 мм
- Axis-FP-800-6D/1,5-6/45/AL: D1=860 мм; D2=900 мм; Diameter=800 мм; Dn=804 мм; Dv=790 мм; Dy=800 мм; Height=400 мм; L=400 мм; Ld=120 мм; Length=900 мм; Lv=105 мм; Maximum Air Flow=19080.0 м³/ч; Motor=Motor : 1.5kW; N=6; P=440 мм; Power=1500 Вт; W=925 мм; W1=875 мм; Weight=77.00 кг; Width=925 мм; d=12 мм; l=200 мм; l1=-200 мм; n=16; r1=430 мм
- Axis-FP-800-4/6D/1,1/0,3-6/20/AL: D1=860 мм; D2=900 мм; Diameter=800 мм; Dn=804 мм; Dv=790 мм; Dy=800 мм; Height=400 мм; L=400 мм; Ld=120 мм; Length=900 мм; Lv=105 мм; Maximum Air Flow=13320.0 м³/ч; Motor=Motor : 1.1 kW; N=6; P=440 мм; Power=1100 Вт; W=925 мм; W1=875 мм; Weight=58.50 кг; Width=925 мм; d=12 мм; l=200 мм; l1=-200 мм; n=16; r1=430 мм
- Axis-FP-800-4/6D/1,5/0,37-6/25/AL: D1=860 мм; D2=900 мм; Diameter=800 мм; Dn=804 мм; Dv=790 мм; Dy=800 мм; Height=400 мм; L=400 мм; Ld=120 мм; Length=900 мм; Lv=105 мм; Maximum Air Flow=17640.0 м³/ч; Motor=Motor : 1.5kW; N=6; P=440 мм; Power=1500 Вт; W=925 мм; W1=875 мм; Weight=62.50 кг; Width=925 мм; d=12 мм; l=200 мм; l1=-200 мм; n=16; r1=430 мм
- Axis-FP-800-4/6D/2,2/0,7-6/30/AL: D1=860 мм; D2=900 мм; Diameter=800 мм; Dn=804 мм; Dv=790 мм; Dy=800 мм; Height=500 мм; L=500 мм; Ld=150 мм; Length=900 мм; Lv=135 мм; Maximum Air Flow=20880.0 м³/ч; Motor=Motor : 2.2kW; N=6; P=440 мм; Power=2200 Вт; W=925 мм; W1=875 мм; Weight=77.00 кг; Width=925 мм; d=12 мм; l=250 мм; l1=-250 мм; n=16; r1=430 мм
- Axis-FP-800-4/6D/2,2/0,7-6/32,5/AL: D1=860 мм; D2=900 мм; Diameter=800 мм; Dn=804 мм; Dv=790 мм; Dy=800 мм; Height=500 мм; L=500 мм; Ld=150 мм; Length=900 мм; Lv=135 мм; Maximum Air Flow=23040.0 м³/ч; Motor=Motor : 2.2kW; N=6; P=440 мм; Power=2200 Вт; W=925 мм; W1=875 мм; Weight=77.00 кг; Width=925 мм; d=12 мм; l=250 мм; l1=-250 мм; n=16; r1=430 мм
- Axis-FP-800-4/6D/3/1-6/35/AL: D1=860 мм; D2=900 мм; Diameter=800 мм; Dn=804 мм; Dv=790 мм; Dy=800 мм; Height=500 мм; L=500 мм; Ld=150 мм; Length=900 мм; Lv=135 мм; Maximum Air Flow=24840.0 м³/ч; Motor=Motor : 3 kW; N=6; P=440 мм; Power=3000 Вт; W=925 мм; W1=875 мм; Weight=88.00 кг; Width=925 мм; d=12 мм; l=250 мм; l1=-250 мм; n=16; r1=430 мм
- Axis-FP-800-4/6D/3/1-6/37,5/AL: D1=860 мм; D2=900 мм; Diameter=800 мм; Dn=804 мм; Dv=790 мм; Dy=800 мм; Height=500 мм; L=500 мм; Ld=150 мм; Length=900 мм; Lv=135 мм; Maximum Air Flow=25920.0 м³/ч; Motor=Motor : 3 kW; N=6; P=440 мм; Power=3000 Вт; W=925 мм; W1=875 мм; Weight=88.00 кг; Width=925 мм; d=12 мм; l=250 мм; l1=-250 мм; n=16; r1=430 мм
- Axis-FP-800-4/6D/4,5/1,5-6/45/AL: D1=860 мм; D2=900 мм; Diameter=800 мм; Dn=804 мм; Dv=790 мм; Dy=800 мм; Height=550 мм; L=550 мм; Ld=165 мм; Length=900 мм; Lv=150 мм; Maximum Air Flow=25920.0 м³/ч; Motor=Motor : 4.4 kW; N=6; P=440 мм; Power=4500 Вт; W=925 мм; W1=875 мм; Weight=125.00 кг; Width=925 мм; d=12 мм; l=275 мм; l1=-275 мм; n=16; r1=430 мм
- Axis-FP-800-4/8D/1,2/0,3-6/20/AL: D1=860 мм; D2=900 мм; Diameter=800 мм; Dn=804 мм; Dv=790 мм; Dy=800 мм; Height=400 мм; L=400 мм; Ld=120 мм; Length=900 мм; Lv=105 мм; Maximum Air Flow=13680.0 м³/ч; Motor=Motor : 1.1 kW; N=6; P=440 мм; Power=1200 Вт; W=925 мм; W1=875 мм; Weight=62.50 кг; Width=925 мм; d=12 мм; l=200 мм; l1=-200 мм; n=16; r1=430 мм
- Axis-FP-800-4/8D/1,6/0,4-6/25/AL: D1=860 мм; D2=900 мм; Diameter=800 мм; Dn=804 мм; Dv=790 мм; Dy=800 мм; Height=400 мм; L=400 мм; Ld=120 мм; Length=900 мм; Lv=105 мм; Maximum Air Flow=18000.0 м³/ч; Motor=Motor : 1.5kW; N=6; P=440 мм; Power=1600 Вт; W=925 мм; W1=875 мм; Weight=65.50 кг; Width=925 мм; d=12 мм; l=200 мм; l1=-200 мм; n=16; r1=430 мм
- Axis-FP-800-4/8D/2,2/0,55-6/30/AL: D1=860 мм; D2=900 мм; Diameter=800 мм; Dn=804 мм; Dv=790 мм; Dy=800 мм; Height=500 мм; L=500 мм; Ld=150 мм; Length=900 мм; Lv=135 мм; Maximum Air Flow=20880.0 м³/ч; Motor=Motor : 2.2kW; N=6; P=440 мм; Power=2200 Вт; W=925 мм; W1=875 мм; Weight=80.00 кг; Width=925 мм; d=12 мм; l=250 мм; l1=-250 мм; n=16; r1=430 мм
- Axis-FP-800-4/8D/2,8/0,7-6/32,5/AL: D1=860 мм; D2=900 мм; Diameter=800 мм; Dn=804 мм; Dv=790 мм; Dy=800 мм; Height=500 мм; L=500 мм; Ld=150 мм; Length=900 мм; Lv=135 мм; Maximum Air Flow=22860.0 м³/ч; Motor=Motor : 2.8 kW; N=6; P=440 мм; Power=2800 Вт; W=925 мм; W1=875 мм; Weight=83.00 кг; Width=925 мм; d=12 мм; l=250 мм; l1=-250 мм; n=16; r1=430 мм
- Axis-FP-800-4/8D/2,8/0,7-6/35/AL: D1=860 мм; D2=900 мм; Diameter=800 мм; Dn=804 мм; Dv=790 мм; Dy=800 мм; Height=500 мм; L=500 мм; Ld=150 мм; Length=900 мм; Lv=135 мм; Maximum Air Flow=24840.0 м³/ч; Motor=Motor : 2.8 kW; N=6; P=440 мм; Power=2800 Вт; W=925 мм; W1=875 мм; Weight=83.00 кг; Width=925 мм; d=12 мм; l=250 мм; l1=-250 мм; n=16; r1=430 мм
- Axis-FP-800-4/8D/3,8/1-6/37,5/AL: D1=860 мм; D2=900 мм; Diameter=800 мм; Dn=804 мм; Dv=790 мм; Dy=800 мм; Height=500 мм; L=500 мм; Ld=150 мм; Length=900 мм; Lv=135 мм; Maximum Air Flow=25920.0 м³/ч; Motor=Motor : 4 kW; N=6; P=440 мм; Power=3800 Вт; W=925 мм; W1=875 мм; Weight=95.00 кг; Width=925 мм; d=12 мм; l=250 мм; l1=-250 мм; n=16; r1=430 мм
- Axis-FP-800-4/8D/3,8/1-6/40/AL: D1=860 мм; D2=900 мм; Diameter=800 мм; Dn=804 мм; Dv=790 мм; Dy=800 мм; Height=500 мм; L=500 мм; Ld=150 мм; Length=900 мм; Lv=135 мм; Maximum Air Flow=27000.0 м³/ч; Motor=Motor : 4 kW; N=6; P=440 мм; Power=3800 Вт; W=925 мм; W1=875 мм; Weight=95.00 кг; Width=925 мм; d=12 мм; l=250 мм; l1=-250 мм; n=16; r1=430 мм
- Axis-FP-800-4/8D/5/1,3-6/45/AL: D1=860 мм; D2=900 мм; Diameter=800 мм; Dn=804 мм; Dv=790 мм; Dy=800 мм; Height=550 мм; L=550 мм; Ld=165 мм; Length=900 мм; Lv=150 мм; Maximum Air Flow=28800.0 м³/ч; Motor=Motor : 5 kW; N=6; P=440 мм; Power=5000 Вт; W=925 мм; W1=875 мм; Weight=125.00 кг; Width=925 мм; d=12 мм; l=275 мм; l1=-275 мм; n=16; r1=430 мм
- Axis-FP-900-4D/4-8/28,5/AL: D1=970 мм; D2=1015 мм; Diameter=900 мм; Dn=904 мм; Dv=890 мм; Dy=900 мм; Height=550 мм; L=550 мм; Ld=165 мм; Length=1015 мм; Lv=150 мм; Maximum Air Flow=28080.0 м³/ч; Motor=Motor : 4 kW; N=8; P=490 мм; Power=4000 Вт; W=1025 мм; W1=975 мм; Weight=97.00 кг; Width=1025 мм; d=15 мм; l=275 мм; l1=-275 мм; n=16; r1=485 мм
- Axis-FP-900-4D/5,5-8/33,5/AL: D1=970 мм; D2=1015 мм; Diameter=900 мм; Dn=904 мм; Dv=890 мм; Dy=900 мм; Height=600 мм; L=600 мм; Ld=180 мм; Length=1015 мм; Lv=165 мм; Maximum Air Flow=33120.0 м³/ч; Motor=Motor : 5.5 kW; N=8; P=490 мм; Power=5500 Вт; W=1025 мм; W1=975 мм; Weight=132.50 кг; Width=1025 мм; d=15 мм; l=300 мм; l1=-300 мм; n=16; r1=485 мм
- Axis-FP-900-4D/7,5-8/40/AL: D1=970 мм; D2=1015 мм; Diameter=900 мм; Dn=904 мм; Dv=890 мм; Dy=900 мм; Height=600 мм; L=600 мм; Ld=180 мм; Length=1015 мм; Lv=165 мм; Maximum Air Flow=37800.0 м³/ч; Motor=Motor : 7.5 kW; N=8; P=490 мм; Power=7500 Вт; W=1025 мм; W1=975 мм; Weight=150.00 кг; Width=1025 мм; d=15 мм; l=300 мм; l1=-300 мм; n=16; r1=485 мм
- Axis-FP-900-4D/11-8/45/AL: D1=970 мм; D2=1015 мм; Diameter=900 мм; Dn=904 мм; Dv=890 мм; Dy=900 мм; Height=600 мм; L=600 мм; Ld=180 мм; Length=1015 мм; Lv=165 мм; Maximum Air Flow=42120.0 м³/ч; Motor=Motor : 11 kW; N=8; P=490 мм; Power=11000 Вт; W=1025 мм; W1=975 мм; Weight=168.50 кг; Width=1025 мм; d=15 мм; l=300 мм; l1=-300 мм; n=16; r1=485 мм
- Axis-FP-900-6D/0,75-8/23,5/AL: D1=970 мм; D2=1015 мм; Diameter=900 мм; Dn=904 мм; Dv=890 мм; Dy=900 мм; Height=450 мм; L=450 мм; Ld=135 мм; Length=1015 мм; Lv=120 мм; Maximum Air Flow=15120.0 м³/ч; Motor=Motor : 0.75 kW; N=8; P=490 мм; Power=750 Вт; W=1025 мм; W1=975 мм; Weight=71.50 кг; Width=1025 мм; d=15 мм; l=225 мм; l1=-225 мм; n=16; r1=485 мм
- Axis-FP-900-6D/1,1-8/28,5/AL: D1=970 мм; D2=1015 мм; Diameter=900 мм; Dn=904 мм; Dv=890 мм; Dy=900 мм; Height=450 мм; L=450 мм; Ld=135 мм; Length=1015 мм; Lv=120 мм; Maximum Air Flow=18900.0 м³/ч; Motor=Motor : 1.1 kW; N=8; P=490 мм; Power=1100 Вт; W=1025 мм; W1=975 мм; Weight=75.50 кг; Width=1025 мм; d=15 мм; l=225 мм; l1=-225 мм; n=16; r1=485 мм
- Axis-FP-900-6D/1,5-8/33,5/AL: D1=970 мм; D2=1015 мм; Diameter=900 мм; Dn=904 мм; Dv=890 мм; Dy=900 мм; Height=550 мм; L=550 мм; Ld=165 мм; Length=1015 мм; Lv=150 мм; Maximum Air Flow=21960.0 м³/ч; Motor=Motor : 1.5kW; N=8; P=490 мм; Power=1500 Вт; W=1025 мм; W1=975 мм; Weight=89.00 кг; Width=1025 мм; d=15 мм; l=275 мм; l1=-275 мм; n=16; r1=485 мм
- Axis-FP-900-6D/2,2-8/41/AL: D1=970 мм; D2=1015 мм; Diameter=900 мм; Dn=904 мм; Dv=890 мм; Dy=900 мм; Height=550 мм; L=550 мм; Ld=165 мм; Length=1015 мм; Lv=150 мм; Maximum Air Flow=25560.0 м³/ч; Motor=Motor : 2.2kW; N=8; P=490 мм; Power=2200 Вт; W=1025 мм; W1=975 мм; Weight=101.00 кг; Width=1025 мм; d=15 мм; l=275 мм; l1=-275 мм; n=16; r1=485 мм
- Axis-FP-900-6D/3-8/45/AL: D1=970 мм; D2=1015 мм; Diameter=900 мм; Dn=904 мм; Dv=890 мм; Dy=900 мм; Height=600 мм; L=600 мм; Ld=180 мм; Length=1015 мм; Lv=165 мм; Maximum Air Flow=27540.0 м³/ч; Motor=Motor : 3 kW; N=8; P=490 мм; Power=3000 Вт; W=1025 мм; W1=975 мм; Weight=104.50 кг; Width=1025 мм; d=15 мм; l=300 мм; l1=-300 мм; n=16; r1=485 мм
- Axis-FP-900-4/6D/3/1-8/23,5/AL: D1=970 мм; D2=1015 мм; Diameter=900 мм; Dn=904 мм; Dv=890 мм; Dy=900 мм; Height=550 мм; L=550 мм; Ld=165 мм; Length=1015 мм; Lv=150 мм; Maximum Air Flow=23040.0 м³/ч; Motor=Motor : 3 kW; N=8; P=490 мм; Power=3000 Вт; W=1025 мм; W1=975 мм; Weight=100.00 кг; Width=1025 мм; d=15 мм; l=275 мм; l1=-275 мм; n=16; r1=485 мм
- Axis-FP-900-4/6D/4,5/1,5-8/28,5/AL: D1=970 мм; D2=1015 мм; Diameter=900 мм; Dn=904 мм; Dv=890 мм; Dy=900 мм; Height=600 мм; L=600 мм; Ld=180 мм; Length=1015 мм; Lv=165 мм; Maximum Air Flow=28080.0 м³/ч; Motor=Motor : 4.4 kW; N=8; P=490 мм; Power=4500 Вт; W=1025 мм; W1=975 мм; Weight=153.50 кг; Width=1025 мм; d=15 мм; l=300 мм; l1=-300 мм; n=16; r1=485 мм
- Axis-FP-900-4/6D/6/2,2-8/33,5/AL: D1=970 мм; D2=1015 мм; Diameter=900 мм; Dn=904 мм; Dv=890 мм; Dy=900 мм; Height=600 мм; L=600 мм; Ld=180 мм; Length=1015 мм; Lv=165 мм; Maximum Air Flow=32400.0 м³/ч; Motor=Motor : 6 kW; N=8; P=490 мм; Power=6000 Вт; W=1025 мм; W1=975 мм; Weight=164.50 кг; Width=1025 мм; d=15 мм; l=300 мм; l1=-300 мм; n=16; r1=485 мм
- Axis-FP-900-4/6D/10/3,3-8/45/AL: D1=970 мм; D2=1015 мм; Diameter=900 мм; Dn=904 мм; Dv=890 мм; Dy=900 мм; Height=750 мм; L=750 мм; Ld=225 мм; Length=1015 мм; Lv=210 мм; Maximum Air Flow=41400.0 м³/ч; Motor=Motor : 11 kW; N=8; P=490 мм; Power=10000 Вт; W=1025 мм; W1=975 мм; Weight=227.50 кг; Width=1025 мм; d=15 мм; l=375 мм; l1=-375 мм; n=17; r1=485 мм
- Axis-FP-900-4/8D/2,8/0,7-8/23,5/AL: D1=970 мм; D2=1015 мм; Diameter=900 мм; Dn=904 мм; Dv=890 мм; Dy=900 мм; Height=550 мм; L=550 мм; Ld=165 мм; Length=1015 мм; Lv=150 мм; Maximum Air Flow=23400.0 м³/ч; Motor=Motor : 2.8 kW; N=8; P=490 мм; Power=2800 Вт; W=1025 мм; W1=975 мм; Weight=95.00 кг; Width=1025 мм; d=15 мм; l=275 мм; l1=-275 мм; n=17; r1=485 мм
- Axis-FP-900-4/8D/3,8/1-8/28,5/AL: D1=970 мм; D2=1015 мм; Diameter=900 мм; Dn=904 мм; Dv=890 мм; Dy=900 мм; Height=550 мм; L=550 мм; Ld=165 мм; Length=1015 мм; Lv=150 мм; Maximum Air Flow=28080.0 м³/ч; Motor=Motor : 4 kW; N=8; P=490 мм; Power=3800 Вт; W=1025 мм; W1=975 мм; Weight=107.00 кг; Width=1025 мм; d=15 мм; l=275 мм; l1=-275 мм; n=17; r1=485 мм
- Axis-FP-900-4/8D/5/1,3-8/33,5/AL: D1=970 мм; D2=1015 мм; Diameter=900 мм; Dn=904 мм; Dv=890 мм; Dy=900 мм; Height=600 мм; L=600 мм; Ld=180 мм; Length=1015 мм; Lv=165 мм; Maximum Air Flow=32760.0 м³/ч; Motor=Motor : 5 kW; N=8; P=490 мм; Power=5000 Вт; W=1025 мм; W1=975 мм; Weight=153.50 кг; Width=1025 мм; d=15 мм; l=300 мм; l1=-300 мм; n=17; r1=485 мм
- Axis-FP-900-4/8D/7,2/1,8-8/40/AL: D1=970 мм; D2=1015 мм; Diameter=900 мм; Dn=904 мм; Dv=890 мм; Dy=900 мм; Height=600 мм; L=600 мм; Ld=180 мм; Length=1015 мм; Lv=165 мм; Maximum Air Flow=37800.0 м³/ч; Motor=Motor : 7.5 kW; N=8; P=490 мм; Power=7200 Вт; W=1025 мм; W1=975 мм; Weight=165.50 кг; Width=1025 мм; d=15 мм; l=300 мм; l1=-300 мм; n=17; r1=485 мм
- Axis-FP-900-4/8D/11/3-8/45/AL: D1=970 мм; D2=1015 мм; Diameter=900 мм; Dn=904 мм; Dv=890 мм; Dy=900 мм; Height=750 мм; L=750 мм; Ld=225 мм; Length=1015 мм; Lv=210 мм; Maximum Air Flow=41400.0 м³/ч; Motor=Motor : 11 kW; N=8; P=490 мм; Power=11000 Вт; W=1025 мм; W1=975 мм; Weight=226.50 кг; Width=1025 мм; d=15 мм; l=375 мм; l1=-375 мм; n=17; r1=485 мм
- Axis-FP-1000-4D/7,5-6/30/AL: D1=1070 мм; D2=1115 мм; Diameter=1000 мм; Dn=1004 мм; Dv=990 мм; Dy=1000 мм; Height=600 мм; L=600 мм; Ld=180 мм; Length=1115 мм; Lv=165 мм; Maximum Air Flow=45360.0 м³/ч; Motor=Motor : 7.5 kW; N=6; P=540 мм; Power=7500 Вт; W=1140 мм; W1=1090 мм; Weight=165.00 кг; Width=1140 мм; d=15 мм; l=300 мм; l1=-300 мм; n=16; r1=535 мм
- Axis-FP-1000-4D/9,2-6/33/AL: D1=1070 мм; D2=1115 мм; Diameter=1000 мм; Dn=1004 мм; Dv=990 мм; Dy=1000 мм; Height=600 мм; L=600 мм; Ld=180 мм; Length=1115 мм; Lv=165 мм; Maximum Air Flow=50040.0 м³/ч; Motor=Motor : 9.2 kW; N=6; P=540 мм; Power=9200 Вт; W=1140 мм; W1=1090 мм; Weight=170.50 кг; Width=1140 мм; d=15 мм; l=300 мм; l1=-300 мм; n=16; r1=535 мм
- Axis-FP-1000-4D/11-6/36/AL: D1=1070 мм; D2=1115 мм; Diameter=1000 мм; Dn=1004 мм; Dv=990 мм; Dy=1000 мм; Height=600 мм; L=600 мм; Ld=180 мм; Length=1115 мм; Lv=165 мм; Maximum Air Flow=52920.0 м³/ч; Motor=Motor : 11 kW; N=6; P=540 мм; Power=11000 Вт; W=1140 мм; W1=1090 мм; Weight=183.50 кг; Width=1140 мм; d=15 мм; l=300 мм; l1=-300 мм; n=16; r1=535 мм
- Axis-FP-1000-4D/15-6/43/AL: D1=1070 мм; D2=1115 мм; Diameter=1000 мм; Dn=1004 мм; Dv=990 мм; Dy=1000 мм; Height=750 мм; L=750 мм; Ld=225 мм; Length=1115 мм; Lv=210 мм; Maximum Air Flow=59040.0 м³/ч; Motor=Motor : 15 kW; N=6; P=540 мм; Power=15000 Вт; W=1140 мм; W1=1090 мм; Weight=244.00 кг; Width=1140 мм; d=15 мм; l=375 мм; l1=-375 мм; n=16; r1=535 мм
- Axis-FP-1000-4D/18,5-6/48/AL: D1=1070 мм; D2=1115 мм; Diameter=1000 мм; Dn=1004 мм; Dv=990 мм; Dy=1000 мм; Height=750 мм; L=750 мм; Ld=225 мм; Length=1115 мм; Lv=210 мм; Maximum Air Flow=61920.0 м³/ч; Motor=Motor : 18.5 kW; N=6; P=540 мм; Power=18500 Вт; W=1140 мм; W1=1090 мм; Weight=259.00 кг; Width=1140 мм; d=15 мм; l=375 мм; l1=-375 мм; n=16; r1=535 мм
- Axis-FP-1000-6D/1,5-6/23/AL: D1=1070 мм; D2=1115 мм; Diameter=1000 мм; Dn=1004 мм; Dv=990 мм; Dy=1000 мм; Height=550 мм; L=550 мм; Ld=165 мм; Length=1115 мм; Lv=150 мм; Maximum Air Flow=23040.0 м³/ч; Motor=Motor : 1.5kW; N=6; P=540 мм; Power=1500 Вт; W=1140 мм; W1=1090 мм; Weight=101.00 кг; Width=1140 мм; d=15 мм; l=275 мм; l1=-275 мм; n=16; r1=535 мм
- Axis-FP-1000-6D/2,2-6/29/AL: D1=1070 мм; D2=1115 мм; Diameter=1000 мм; Dn=1004 мм; Dv=990 мм; Dy=1000 мм; Height=550 мм; L=550 мм; Ld=165 мм; Length=1115 мм; Lv=150 мм; Maximum Air Flow=29880.0 м³/ч; Motor=Motor : 2.2kW; N=6; P=540 мм; Power=2200 Вт; W=1140 мм; W1=1090 мм; Weight=114.00 кг; Width=1140 мм; d=15 мм; l=275 мм; l1=-275 мм; n=16; r1=535 мм
- Axis-FP-1000-6D/3-6/35/AL: D1=1070 мм; D2=1115 мм; Diameter=1000 мм; Dn=1004 мм; Dv=990 мм; Dy=1000 мм; Height=600 мм; L=600 мм; Ld=180 мм; Length=1115 мм; Lv=165 мм; Maximum Air Flow=34200.0 м³/ч; Motor=Motor : 3 kW; N=6; P=540 мм; Power=3000 Вт; W=1140 мм; W1=1090 мм; Weight=155.50 кг; Width=1140 мм; d=15 мм; l=300 мм; l1=-300 мм; n=16; r1=535 мм
- Axis-FP-1000-6D/4-6/41/AL: D1=1070 мм; D2=1115 мм; Diameter=1000 мм; Dn=1004 мм; Dv=990 мм; Dy=1000 мм; Height=600 мм; L=600 мм; Ld=180 мм; Length=1115 мм; Lv=165 мм; Maximum Air Flow=37800.0 м³/ч; Motor=Motor : 4 kW; N=6; P=540 мм; Power=4000 Вт; W=1140 мм; W1=1090 мм; Weight=159.50 кг; Width=1140 мм; d=15 мм; l=300 мм; l1=-300 мм; n=16; r1=535 мм
- Axis-FP-1000-6D/5,5-6/48/AL: D1=1070 мм; D2=1115 мм; Diameter=1000 мм; Dn=1004 мм; Dv=990 мм; Dy=1000 мм; Height=600 мм; L=600 мм; Ld=180 мм; Length=1115 мм; Lv=165 мм; Maximum Air Flow=40680.0 м³/ч; Motor=Motor : 5.5 kW; N=6; P=540 мм; Power=5500 Вт; W=1140 мм; W1=1090 мм; Weight=172.50 кг; Width=1140 мм; d=15 мм; l=300 мм; l1=-300 мм; n=16; r1=535 мм
- Axis-FP-1000-4/6D/4,5/1,5-6/20/AL: D1=1070 мм; D2=1115 мм; Diameter=1000 мм; Dn=1004 мм; Dv=990 мм; Dy=1000 мм; Height=600 мм; L=600 мм; Ld=180 мм; Length=1115 мм; Lv=165 мм; Maximum Air Flow=30960.0 м³/ч; Motor=Motor : 4.4 kW; N=6; P=540 мм; Power=4500 Вт; W=1140 мм; W1=1090 мм; Weight=168.50 кг; Width=1140 мм; d=15 мм; l=300 мм; l1=-300 мм; n=16; r1=535 мм
- Axis-FP-1000-4/6D/6/2,2-6/25/AL: D1=1070 мм; D2=1115 мм; Diameter=1000 мм; Dn=1004 мм; Dv=990 мм; Dy=1000 мм; Height=600 мм; L=600 мм; Ld=180 мм; Length=1115 мм; Lv=165 мм; Maximum Air Flow=38880.0 м³/ч; Motor=Motor : 6 kW; N=6; P=540 мм; Power=6000 Вт; W=1140 мм; W1=1090 мм; Weight=179.50 кг; Width=1140 мм; d=15 мм; l=300 мм; l1=-300 мм; n=16; r1=535 мм
- Axis-FP-1000-4/6D/10/3,3-6/34/AL: D1=1070 мм; D2=1115 мм; Diameter=1000 мм; Dn=1004 мм; Dv=990 мм; Dy=1000 мм; Height=750 мм; L=750 мм; Ld=225 мм; Length=1115 мм; Lv=210 мм; Maximum Air Flow=50400.0 м³/ч; Motor=Motor : 10 kW; N=6; P=540 мм; Power=10000 Вт; W=1140 мм; W1=1090 мм; Weight=244.50 кг; Width=1140 мм; d=15 мм; l=375 мм; l1=-375 мм; n=16; r1=535 мм
- Axis-FP-1000-4/6D/14/4,5-6/41/AL: D1=1070 мм; D2=1115 мм; Diameter=1000 мм; Dn=1004 мм; Dv=990 мм; Dy=1000 мм; Height=750 мм; L=750 мм; Ld=225 мм; Length=1115 мм; Lv=210 мм; Maximum Air Flow=57960.0 м³/ч; Motor=Motor : 14 kW; N=6; P=540 мм; Power=14000 Вт; W=1140 мм; W1=1090 мм; Weight=259.50 кг; Width=1140 мм; d=15 мм; l=375 мм; l1=-375 мм; n=16; r1=535 мм
- Axis-FP-1000-4/6D/16/6,5-6/45/AL: D1=1070 мм; D2=1115 мм; Diameter=1000 мм; Dn=1004 мм; Dv=990 мм; Dy=1000 мм; Height=800 мм; L=800 мм; Ld=240 мм; Length=1115 мм; Lv=225 мм; Maximum Air Flow=60480.0 м³/ч; Motor=Motor : 16 kW; N=6; P=540 мм; Power=16000 Вт; W=1140 мм; W1=1090 мм; Weight=328.00 кг; Width=1140 мм; d=15 мм; l=400 мм; l1=-400 мм; n=16; r1=535 мм
- Axis-FP-1000-4/8D/5/1,3-6/23/AL: D1=1070 мм; D2=1115 мм; Diameter=1000 мм; Dn=1004 мм; Dv=990 мм; Dy=1000 мм; Height=600 мм; L=600 мм; Ld=180 мм; Length=1115 мм; Lv=165 мм; Maximum Air Flow=34920.0 м³/ч; Motor=Motor : 5 kW; N=6; P=540 мм; Power=5000 Вт; W=1140 мм; W1=1090 мм; Weight=168.50 кг; Width=1140 мм; d=15 мм; l=300 мм; l1=-300 мм; n=16; r1=535 мм
- Axis-FP-1000-4/8D/7,2/1,8-6/29/AL: D1=1070 мм; D2=1115 мм; Diameter=1000 мм; Dn=1004 мм; Dv=990 мм; Dy=1000 мм; Height=600 мм; L=600 мм; Ld=180 мм; Length=1115 мм; Lv=165 мм; Maximum Air Flow=45000.0 м³/ч; Motor=Motor : 7.5 kW; N=6; P=540 мм; Power=7200 Вт; W=1140 мм; W1=1090 мм; Weight=180.50 кг; Width=1140 мм; d=15 мм; l=300 мм; l1=-300 мм; n=16; r1=535 мм
- Axis-FP-1000-4/8D/11/3-6/36/AL: D1=1070 мм; D2=1115 мм; Diameter=1000 мм; Dn=1004 мм; Dv=990 мм; Dy=1000 мм; Height=750 мм; L=750 мм; Ld=225 мм; Length=1115 мм; Lv=210 мм; Maximum Air Flow=52920.0 м³/ч; Motor=Motor : 11 kW; N=6; P=540 мм; Power=11000 Вт; W=1140 мм; W1=1090 мм; Weight=243.50 кг; Width=1140 мм; d=15 мм; l=375 мм; l1=-375 мм; n=16; r1=535 мм
- Axis-FP-1000-4/8D/14/3,5-6/41/AL: D1=1070 мм; D2=1115 мм; Diameter=1000 мм; Dn=1004 мм; Dv=990 мм; Dy=1000 мм; Height=750 мм; L=750 мм; Ld=225 мм; Length=1115 мм; Lv=210 мм; Maximum Air Flow=56880.0 м³/ч; Motor=Motor : 14 kW; N=6; P=540 мм; Power=14000 Вт; W=1140 мм; W1=1090 мм; Weight=259.50 кг; Width=1140 мм; d=15 мм; l=375 мм; l1=-375 мм; n=16; r1=535 мм
- Axis-FP-1000-4/8D/17/4,3-6/46/AL: D1=1070 мм; D2=1115 мм; Diameter=1000 мм; Dn=1004 мм; Dv=990 мм; Dy=1000 мм; Height=800 мм; L=800 мм; Ld=240 мм; Length=1115 мм; Lv=225 мм; Maximum Air Flow=59940.0 м³/ч; Motor=Motor : 16 kW; N=6; P=540 мм; Power=17000 Вт; W=1140 мм; W1=1090 мм; Weight=295.00 кг; Width=1140 мм; d=15 мм; l=400 мм; l1=-400 мм; n=16; r1=535 мм
- Axis-FP-1120-4D/9,2-6/27/AL: D1=1190 мм; D2=1270 мм; Diameter=1120 мм; Dn=1124 мм; Dv=1110 мм; Dy=1120 мм; Height=600 мм; L=600 мм; Ld=180 мм; Length=1270 мм; Lv=165 мм; Maximum Air Flow=55440.0 м³/ч; Motor=Motor : 9.2 kW; N=6; P=600 мм; Power=9200 Вт; W=1280 мм; W1=1230 мм; Weight=189.00 кг; Width=1280 мм; d=15 мм; l=300 мм; l1=-300 мм; n=20; r1=595 мм
- Axis-FP-1120-4D/11-6/31/AL: D1=1190 мм; D2=1270 мм; Diameter=1120 мм; Dn=1124 мм; Dv=1110 мм; Dy=1120 мм; Height=600 мм; L=600 мм; Ld=180 мм; Length=1270 мм; Lv=165 мм; Maximum Air Flow=63000.0 м³/ч; Motor=Motor : 11 kW; N=6; P=600 мм; Power=11000 Вт; W=1280 мм; W1=1230 мм; Weight=202.00 кг; Width=1280 мм; d=15 мм; l=300 мм; l1=-300 мм; n=20; r1=595 мм
- Axis-FP-1120-4D/15-6/35/AL: D1=1190 мм; D2=1270 мм; Diameter=1120 мм; Dn=1124 мм; Dv=1110 мм; Dy=1120 мм; Height=750 мм; L=750 мм; Ld=225 мм; Length=1270 мм; Lv=210 мм; Maximum Air Flow=68040.0 м³/ч; Motor=Motor : 15 kW; N=6; P=600 мм; Power=15000 Вт; W=1280 мм; W1=1230 мм; Weight=296.00 кг; Width=1280 мм; d=15 мм; l=375 мм; l1=-375 мм; n=20; r1=595 мм
- Axis-FP-1120-4D/18,5-6/40/AL: D1=1190 мм; D2=1270 мм; Diameter=1120 мм; Dn=1124 мм; Dv=1110 мм; Dy=1120 мм; Height=750 мм; L=750 мм; Ld=225 мм; Length=1270 мм; Lv=210 мм; Maximum Air Flow=73800.0 м³/ч; Motor=Motor : 18.5 kW; N=6; P=600 мм; Power=18500 Вт; W=1280 мм; W1=1230 мм; Weight=312.00 кг; Width=1280 мм; d=15 мм; l=375 мм; l1=-375 мм; n=20; r1=595 мм
- Axis-FP-1120-4D/22-6/43/AL: D1=1190 мм; D2=1270 мм; Diameter=1120 мм; Dn=1124 мм; Dv=1110 мм; Dy=1120 мм; Height=800 мм; L=800 мм; Ld=240 мм; Length=1270 мм; Lv=225 мм; Maximum Air Flow=77760.0 м³/ч; Motor=Motor : 20 kW; N=6; P=600 мм; Power=22000 Вт; W=1280 мм; W1=1230 мм; Weight=352.00 кг; Width=1280 мм; d=15 мм; l=400 мм; l1=-400 мм; n=20; r1=595 мм
- Axis-FP-1120-6D/2,2-6/23/AL: D1=1190 мм; D2=1270 мм; Diameter=1120 мм; Dn=1124 мм; Dv=1110 мм; Dy=1120 мм; Height=550 мм; L=550 мм; Ld=165 мм; Length=1270 мм; Lv=150 мм; Maximum Air Flow=30960.0 м³/ч; Motor=Motor : 2.2kW; N=6; P=600 мм; Power=2200 Вт; W=1280 мм; W1=1230 мм; Weight=146.00 кг; Width=1280 мм; d=15 мм; l=275 мм; l1=-275 мм; n=20; r1=595 мм
- Axis-FP-1120-6D/3-6/29/AL: D1=1190 мм; D2=1270 мм; Diameter=1120 мм; Dn=1124 мм; Dv=1110 мм; Dy=1120 мм; Height=600 мм; L=600 мм; Ld=180 мм; Length=1270 мм; Lv=165 мм; Maximum Air Flow=39960.0 м³/ч; Motor=Motor : 3 kW; N=6; P=600 мм; Power=3000 Вт; W=1280 мм; W1=1230 мм; Weight=174.00 кг; Width=1280 мм; d=15 мм; l=300 мм; l1=-300 мм; n=20; r1=595 мм
- Axis-FP-1120-6D/4-6/34/AL: D1=1190 мм; D2=1270 мм; Diameter=1120 мм; Dn=1124 мм; Dv=1110 мм; Dy=1120 мм; Height=600 мм; L=600 мм; Ld=180 мм; Length=1270 мм; Lv=165 мм; Maximum Air Flow=43920.0 м³/ч; Motor=Motor : 4 kW; N=6; P=600 мм; Power=4000 Вт; W=1280 мм; W1=1230 мм; Weight=178.00 кг; Width=1280 мм; d=15 мм; l=300 мм; l1=-300 мм; n=20; r1=595 мм
- Axis-FP-1120-6D/5,5-6/40/AL: D1=1190 мм; D2=1270 мм; Diameter=1120 мм; Dn=1124 мм; Dv=1110 мм; Dy=1120 мм; Height=600 мм; L=600 мм; Ld=180 мм; Length=1270 мм; Lv=165 мм; Maximum Air Flow=50040.0 м³/ч; Motor=Motor : 5.5 kW; N=6; P=600 мм; Power=5500 Вт; W=1280 мм; W1=1230 мм; Weight=191.00 кг; Width=1280 мм; d=15 мм; l=300 мм; l1=-300 мм; n=20; r1=595 мм
- Axis-FP-1120-6D/7,5-6/46/AL: D1=1190 мм; D2=1270 мм; Diameter=1120 мм; Dn=1124 мм; Dv=1110 мм; Dy=1120 мм; Height=750 мм; L=750 мм; Ld=225 мм; Length=1270 мм; Lv=210 мм; Maximum Air Flow=52920.0 м³/ч; Motor=Motor : 7.5 kW; N=6; P=600 мм; Power=7500 Вт; W=1280 мм; W1=1230 мм; Weight=280.00 кг; Width=1280 мм; d=15 мм; l=375 мм; l1=-375 мм; n=20; r1=595 мм
- Axis-FP-1120-6D/9,2-6/50/AL: D1=1190 мм; D2=1270 мм; Diameter=1120 мм; Dn=1124 мм; Dv=1110 мм; Dy=1120 мм; Height=750 мм; L=750 мм; Ld=225 мм; Length=1270 мм; Lv=210 мм; Maximum Air Flow=54000.0 м³/ч; Motor=Motor : 9.2 kW; N=6; P=600 мм; Power=9200 Вт; W=1280 мм; W1=1230 мм; Weight=289.00 кг; Width=1280 мм; d=15 мм; l=375 мм; l1=-375 мм; n=20; r1=595 мм
- Axis-FP-1120-4/6D/6/2,2-5/24/AL: D1=1190 мм; D2=1270 мм; Diameter=1120 мм; Dn=1124 мм; Dv=1110 мм; Dy=1120 мм; Height=600 мм; L=600 мм; Ld=180 мм; Length=1270 мм; Lv=165 мм; Maximum Air Flow=45000.0 м³/ч; Motor=Motor : 6 kW; N=6; P=600 мм; Power=6000 Вт; W=1280 мм; W1=1230 мм; Weight=196.00 кг; Width=1280 мм; d=15 мм; l=300 мм; l1=-300 мм; n=20; r1=595 мм
- Axis-FP-1120-4/6D/10/3,3-6/29/AL: D1=1190 мм; D2=1270 мм; Diameter=1120 мм; Dn=1124 мм; Dv=1110 мм; Dy=1120 мм; Height=750 мм; L=750 мм; Ld=225 мм; Length=1270 мм; Lv=210 мм; Maximum Air Flow=57960.0 м³/ч; Motor=Motor : 10 kW; N=6; P=600 мм; Power=10000 Вт; W=1280 мм; W1=1230 мм; Weight=297.00 кг; Width=1280 мм; d=15 мм; l=375 мм; l1=-375 мм; n=20; r1=595 мм
- Axis-FP-1120-4/6D/14/4,5-6/34/AL: D1=1190 мм; D2=1270 мм; Diameter=1120 мм; Dn=1124 мм; Dv=1110 мм; Dy=1120 мм; Height=750 мм; L=750 мм; Ld=225 мм; Length=1270 мм; Lv=210 мм; Maximum Air Flow=65880.0 м³/ч; Motor=Motor : 14 kW; N=6; P=600 мм; Power=14000 Вт; W=1280 мм; W1=1230 мм; Weight=312.00 кг; Width=1280 мм; d=15 мм; l=375 мм; l1=-375 мм; n=20; r1=595 мм
- Axis-FP-1120-4/6D/16/6,5-6/37/AL: D1=1190 мм; D2=1270 мм; Diameter=1120 мм; Dn=1124 мм; Dv=1110 мм; Dy=1120 мм; Height=800 мм; L=800 мм; Ld=240 мм; Length=1270 мм; Lv=225 мм; Maximum Air Flow=69840.0 м³/ч; Motor=Motor : 16 kW; N=6; P=600 мм; Power=16000 Вт; W=1280 мм; W1=1230 мм; Weight=384.00 кг; Width=1280 мм; d=15 мм; l=400 мм; l1=-400 мм; n=20; r1=595 мм
- Axis-FP-1120-4/6D/20/8,5-6/41/AL: D1=1190 мм; D2=1270 мм; Diameter=1120 мм; Dn=1124 мм; Dv=1110 мм; Dy=1120 мм; Height=800 мм; L=800 мм; Ld=240 мм; Length=1270 мм; Lv=225 мм; Maximum Air Flow=74880.0 м³/ч; Motor=Motor : 20 kW; N=6; P=600 мм; Power=20000 Вт; W=1280 мм; W1=1230 мм; Weight=387.00 кг; Width=1280 мм; d=15 мм; l=400 мм; l1=-400 мм; n=20; r1=595 мм
- Axis-FP-1120-4/8D/7,2/1,8-6/23/AL: D1=1190 мм; D2=1270 мм; Diameter=1120 мм; Dn=1124 мм; Dv=1110 мм; Dy=1120 мм; Height=600 мм; L=600 мм; Ld=180 мм; Length=1270 мм; Lv=165 мм; Maximum Air Flow=46800.0 м³/ч; Motor=Motor : 7.5 kW; N=6; P=600 мм; Power=7200 Вт; W=1280 мм; W1=1230 мм; Weight=199.00 кг; Width=1280 мм; d=15 мм; l=300 мм; l1=-300 мм; n=20; r1=595 мм
- Axis-FP-1120-4/8D/11/3-6/31/AL: D1=1190 мм; D2=1270 мм; Diameter=1120 мм; Dn=1124 мм; Dv=1110 мм; Dy=1120 мм; Height=750 мм; L=750 мм; Ld=225 мм; Length=1270 мм; Lv=210 мм; Maximum Air Flow=61920.0 м³/ч; Motor=Motor : 11 kW; N=6; P=600 мм; Power=11000 Вт; W=1280 мм; W1=1230 мм; Weight=296.00 кг; Width=1280 мм; d=15 мм; l=375 мм; l1=-375 мм; n=20; r1=595 мм
- Axis-FP-1120-4/8D/14/3,5-6/34/AL: D1=1190 мм; D2=1270 мм; Diameter=1120 мм; Dn=1124 мм; Dv=1110 мм; Dy=1120 мм; Height=750 мм; L=750 мм; Ld=225 мм; Length=1270 мм; Lv=210 мм; Maximum Air Flow=64800.0 м³/ч; Motor=Motor : 14 kW; N=6; P=600 мм; Power=14000 Вт; W=1280 мм; W1=1230 мм; Weight=312.00 кг; Width=1280 мм; d=15 мм; l=375 мм; l1=-375 мм; n=20; r1=595 мм
- Axis-FP-1120-4/8D/17/4,3-6/38/AL: D1=1190 мм; D2=1270 мм; Diameter=1120 мм; Dn=1124 мм; Dv=1110 мм; Dy=1120 мм; Height=800 мм; L=800 мм; Ld=240 мм; Length=1270 мм; Lv=225 мм; Maximum Air Flow=72000.0 м³/ч; Motor=Motor : 16 kW; N=6; P=600 мм; Power=17000 Вт; W=1280 мм; W1=1230 мм; Weight=351.00 кг; Width=1280 мм; d=15 мм; l=400 мм; l1=-400 мм; n=20; r1=595 мм
- Axis-FP-1120-4/8D/20/5-6/41/AL: D1=1190 мм; D2=1270 мм; Diameter=1120 мм; Dn=1124 мм; Dv=1110 мм; Dy=1120 мм; Height=800 мм; L=800 мм; Ld=240 мм; Length=1270 мм; Lv=225 мм; Maximum Air Flow=72000.0 м³/ч; Motor=Motor : 20 kW; N=6; P=600 мм; Power=20000 Вт; W=1280 мм; W1=1230 мм; Weight=379.00 кг; Width=1280 мм; d=15 мм; l=400 мм; l1=-400 мм; n=20; r1=595 мм
- Axis-FP-1250-4D/22-8/28/AL: D1=1320 мм; D2=1400 мм; Diameter=1250 мм; Dn=1254 мм; Dv=1240 мм; Dy=1250 мм; Height=800 мм; L=800 мм; Ld=240 мм; Length=1400 мм; Lv=225 мм; Maximum Air Flow=86040.0 м³/ч; Motor=Motor : 20 kW; N=8; P=665 мм; Power=22000 Вт; W=1450 мм; W1=1400 мм; Weight=377.50 кг; Width=1450 мм; d=15 мм; l=400 мм; l1=-400 мм; n=20; r1=660 мм
- Axis-FP-1250-4D/30-8/34/AL: D1=1320 мм; D2=1400 мм; Diameter=1250 мм; Dn=1254 мм; Dv=1240 мм; Dy=1250 мм; Height=800 мм; L=800 мм; Ld=240 мм; Length=1400 мм; Lv=225 мм; Maximum Air Flow=99720.0 м³/ч; Motor=Motor : 28 kW; N=8; P=665 мм; Power=30000 Вт; W=1450 мм; W1=1400 мм; Weight=403.50 кг; Width=1450 мм; d=15 мм; l=400 мм; l1=-400 мм; n=20; r1=660 мм
- Axis-FP-1250-6D/5,5-8/23/AL: D1=1320 мм; D2=1400 мм; Diameter=1250 мм; Dn=1254 мм; Dv=1240 мм; Dy=1250 мм; Height=600 мм; L=600 мм; Ld=180 мм; Length=1400 мм; Lv=165 мм; Maximum Air Flow=47880.0 м³/ч; Motor=Motor : 5.5 kW; N=8; P=665 мм; Power=5500 Вт; W=1450 мм; W1=1400 мм; Weight=231.00 кг; Width=1450 мм; d=15 мм; l=300 мм; l1=-300 мм; n=20; r1=660 мм
- Axis-FP-1250-6D/7,5-8/30/AL: D1=1320 мм; D2=1400 мм; Diameter=1250 мм; Dn=1254 мм; Dv=1240 мм; Dy=1250 мм; Height=750 мм; L=750 мм; Ld=225 мм; Length=1400 мм; Lv=210 мм; Maximum Air Flow=60840.0 м³/ч; Motor=Motor : 7.5 kW; N=8; P=665 мм; Power=7500 Вт; W=1450 мм; W1=1400 мм; Weight=303.00 кг; Width=1450 мм; d=15 мм; l=375 мм; l1=-375 мм; n=20; r1=660 мм
- Axis-FP-1250-6D/9,2-8/34/AL: D1=1320 мм; D2=1400 мм; Diameter=1250 мм; Dn=1254 мм; Dv=1240 мм; Dy=1250 мм; Height=750 мм; L=750 мм; Ld=225 мм; Length=1400 мм; Lv=210 мм; Maximum Air Flow=66960.0 м³/ч; Motor=Motor : 9.2 kW; N=8; P=665 мм; Power=9200 Вт; W=1450 мм; W1=1400 мм; Weight=303.00 кг; Width=1450 мм; d=15 мм; l=375 мм; l1=-375 мм; n=20; r1=660 мм
- Axis-FP-1250-6D/11-8/38/AL: D1=1320 мм; D2=1400 мм; Diameter=1250 мм; Dn=1254 мм; Dv=1240 мм; Dy=1250 мм; Height=750 мм; L=750 мм; Ld=225 мм; Length=1400 мм; Lv=210 мм; Maximum Air Flow=72000.0 м³/ч; Motor=Motor : 11 kW; N=8; P=665 мм; Power=11000 Вт; W=1450 мм; W1=1400 мм; Weight=327.00 кг; Width=1450 мм; d=15 мм; l=375 мм; l1=-375 мм; n=20; r1=660 мм
- Axis-FP-1250-4/6D/16/6,5-8/20/AL: D1=1320 мм; D2=1400 мм; Diameter=1250 мм; Dn=1254 мм; Dv=1240 мм; Dy=1250 мм; Height=800 мм; L=800 мм; Ld=240 мм; Length=1400 мм; Lv=225 мм; Maximum Air Flow=63000.0 м³/ч; Motor=Motor : 16 kW; N=8; P=665 мм; Power=16000 Вт; W=1450 мм; W1=1400 мм; Weight=408.50 кг; Width=1450 мм; d=15 мм; l=400 мм; l1=-400 мм; n=20; r1=660 мм
- Axis-FP-1250-4/6D/20/8,5-8/25/AL: D1=1320 мм; D2=1400 мм; Diameter=1250 мм; Dn=1254 мм; Dv=1240 мм; Dy=1250 мм; Height=800 мм; L=800 мм; Ld=240 мм; Length=1400 мм; Lv=225 мм; Maximum Air Flow=77940.0 м³/ч; Motor=Motor : 20 kW; N=8; P=665 мм; Power=20000 Вт; W=1450 мм; W1=1400 мм; Weight=411.50 кг; Width=1450 мм; d=15 мм; l=400 мм; l1=-400 мм; n=20; r1=660 мм
- Axis-FP-1250-4/6D/26/9-8/31/AL: D1=1320 мм; D2=1400 мм; Diameter=1250 мм; Dn=1254 мм; Dv=1240 мм; Dy=1250 мм; Height=850 мм; L=850 мм; Ld=255 мм; Length=1400 мм; Lv=240 мм; Maximum Air Flow=92880.0 м³/ч; Motor=Motor : 28 kW; N=8; P=665 мм; Power=26000 Вт; W=1450 мм; W1=1400 мм; Weight=510.00 кг; Width=1450 мм; d=15 мм; l=425 мм; l1=-425 мм; n=20; r1=660 мм
- Axis-FP-1250-4/8D/17/4,3-8/21/AL: D1=1320 мм; D2=1400 мм; Diameter=1250 мм; Dn=1254 мм; Dv=1240 мм; Dy=1250 мм; Height=800 мм; L=800 мм; Ld=240 мм; Length=1400 мм; Lv=225 мм; Maximum Air Flow=66960.0 м³/ч; Motor=Motor : 16 kW; N=8; P=665 мм; Power=17000 Вт; W=1450 мм; W1=1400 мм; Weight=375.50 кг; Width=1450 мм; d=15 мм; l=400 мм; l1=-400 мм; n=20; r1=660 мм
- Axis-FP-1250-4/8D/20/5-8/25/AL: D1=1320 мм; D2=1400 мм; Diameter=1250 мм; Dn=1254 мм; Dv=1240 мм; Dy=1250 мм; Height=800 мм; L=800 мм; Ld=240 мм; Length=1400 мм; Lv=225 мм; Maximum Air Flow=77760.0 м³/ч; Motor=Motor : 20 kW; N=8; P=665 мм; Power=20000 Вт; W=1450 мм; W1=1400 мм; Weight=403.50 кг; Width=1450 мм; d=15 мм; l=400 мм; l1=-400 мм; n=20; r1=660 мм
- Axis-FP-1250-4/8D/28/6,5-8/32/AL: D1=1320 мм; D2=1400 мм; Diameter=1250 мм; Dn=1254 мм; Dv=1240 мм; Dy=1250 мм; Height=850 мм; L=850 мм; Ld=255 мм; Length=1400 мм; Lv=240 мм; Maximum Air Flow=95040.0 м³/ч; Motor=Motor : 28 kW; N=8; P=665 мм; Power=28000 Вт; W=1450 мм; W1=1400 мм; Weight=465.00 кг; Width=1450 мм; d=15 мм; l=425 мм; l1=-425 мм; n=20; r1=660 мм
